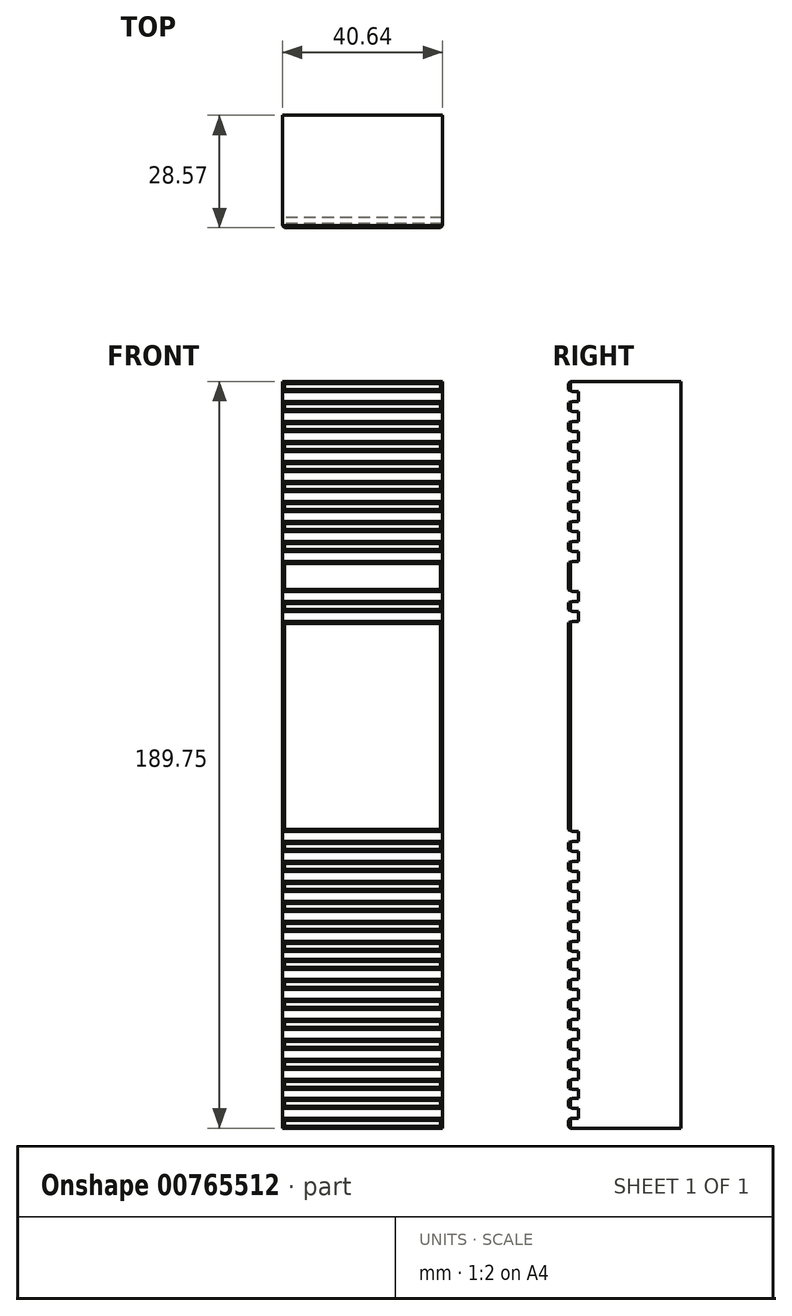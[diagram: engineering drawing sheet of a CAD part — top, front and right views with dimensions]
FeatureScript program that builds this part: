
annotation { "Feature Type Name" : "Feature", "Feature Type Description" : "" }
export const myFeature = defineFeature(function(context is Context, id is Id, definition is map)
    precondition{}
    {
        {
            var Q0;
            Q0=qCreatedBy(makeId("Top.planeOp"),FACE);
            var sketch = newSketch(context, id + "F0", { "sketchPlane" : qUnion([Q0])});
            skLineSegment(sketch, "E0.bottom", {"start": v(0, 0) * mm, "end": v(40.64, 0) * mm});
            skLineSegment(sketch, "E0.top", {"start": v(0, 35.56) * mm, "end": v(40.64, 35.56) * mm});
            skLineSegment(sketch, "E0.left", {"start": v(0, 0) * mm, "end": v(0, 35.56) * mm});
            skLineSegment(sketch, "E0.right", {"start": v(40.64, 0) * mm, "end": v(40.64, 35.56) * mm});
            skSolve(sketch);
        }
        {
            var Q0;
            Q0=makeQuery(id+"F0.imprint","IMPRINT",FACE,{"disambiguationData":[TD([[makeQuery(id+"F0.imprint","IMPRINT",EDGE,{"derivedFrom":sQuery(id+"F0.wireOp",EDGE,"E0.bottom")}),1.0]])]});
            extrude(context, id + "F1", {"entities" : qUnion([Q0]), "depth" : 190.5 * mm, "offsetDistance" : 25.4 * mm});
        }
        {
            var Q0;
            Q0=makeQuery(id+"F1.opExtrude","SWEPT_FACE",FACE,{"disambiguationData":[OSD([sQuery(id+"F0.wireOp",EDGE,"E0.left")])]});
            var sketch = newSketch(context, id + "F2", { "sketchPlane" : qUnion([Q0])});
            skLineSegment(sketch, "E1", {"start": v(0, 190.5) * mm, "end": v(-2.54, 190.5) * mm});
            skLineSegment(sketch, "E2", {"start": v(-2.54, 190.5) * mm, "end": v(-2.54, 0) * mm});
            skLineSegment(sketch, "E3", {"start": v(0, 190.5) * mm, "end": v(0, 185.42) * mm});
            skLineSegment(sketch, "E4", {"start": v(0, 185.42) * mm, "end": v(-2.54, 185.42) * mm});
            skLineSegment(sketch, "E5", {"start": v(0, 187.96) * mm, "end": v(-2.54, 187.96) * mm});
            skLineSegment(sketch, "E6", {"start": v(0, 185.42) * mm, "end": v(0, 175.26) * mm});
            skLineSegment(sketch, "E7", {"start": v(0, 175.26) * mm, "end": v(-2.54, 175.26) * mm});
            skLineSegment(sketch, "E8", {"start": v(0, 180.34) * mm, "end": v(-2.54, 180.34) * mm});
            skLineSegment(sketch, "E9", {"start": v(-2.54, 185.42) * mm, "end": v(-2.54, 182.88) * mm});
            skLineSegment(sketch, "E10", {"start": v(-2.54, 182.88) * mm, "end": v(0, 182.88) * mm});
            skLineSegment(sketch, "E11", {"start": v(0, 175.26) * mm, "end": v(0, 177.8) * mm});
            skLineSegment(sketch, "E12", {"start": v(0, 177.8) * mm, "end": v(-2.54, 177.8) * mm});
            skLineSegment(sketch, "E13", {"start": v(-2.54, 175.26) * mm, "end": v(-2.54, 170.18) * mm});
            skLineSegment(sketch, "E14", {"start": v(-2.54, 170.18) * mm, "end": v(0, 170.18) * mm});
            skLineSegment(sketch, "E15", {"start": v(0, 170.18) * mm, "end": v(0, 172.72) * mm});
            skPoint(sketch, "E15.endSnap0", {"position": v(-2.54, 172.72) * mm});
            skLineSegment(sketch, "E16", {"start": v(0, 172.72) * mm, "end": v(-2.54, 172.72) * mm});
            skLineSegment(sketch, "E17", {"start": v(-2.54, 170.18) * mm, "end": v(-2.54, 165.1) * mm});
            skLineSegment(sketch, "E18", {"start": v(-2.54, 165.1) * mm, "end": v(0, 165.1) * mm});
            skLineSegment(sketch, "E19", {"start": v(0, 165.1) * mm, "end": v(0, 167.64) * mm});
            skPoint(sketch, "E19.endSnap0", {"position": v(-2.54, 167.64) * mm});
            skLineSegment(sketch, "E20", {"start": v(0, 167.64) * mm, "end": v(-2.54, 167.64) * mm});
            skLineSegment(sketch, "E21", {"start": v(-2.54, 165.1) * mm, "end": v(-2.54, 160.02) * mm});
            skLineSegment(sketch, "E22", {"start": v(-2.54, 160.02) * mm, "end": v(0, 160.02) * mm});
            skLineSegment(sketch, "E23", {"start": v(0, 160.02) * mm, "end": v(0, 162.56) * mm});
            skPoint(sketch, "E23.endSnap0", {"position": v(-2.54, 162.56) * mm});
            skLineSegment(sketch, "E24", {"start": v(0, 162.56) * mm, "end": v(-2.54, 162.56) * mm});
            skLineSegment(sketch, "E25", {"start": v(-2.54, 160.02) * mm, "end": v(-2.54, 154.94) * mm});
            skLineSegment(sketch, "E26", {"start": v(-2.54, 154.94) * mm, "end": v(0, 154.94) * mm});
            skPoint(sketch, "E27.endSnap0", {"position": v(-2.54, 157.48) * mm});
            skLineSegment(sketch, "E28", {"start": v(0, 154.94) * mm, "end": v(0, 157.48) * mm});
            skLineSegment(sketch, "E29", {"start": v(0, 157.48) * mm, "end": v(-2.54, 157.48) * mm});
            skLineSegment(sketch, "E30", {"start": v(-2.54, 154.94) * mm, "end": v(-2.54, 149.86) * mm});
            skLineSegment(sketch, "E31", {"start": v(-2.54, 149.86) * mm, "end": v(0, 149.86) * mm});
            skLineSegment(sketch, "E32", {"start": v(0, 149.86) * mm, "end": v(0, 152.4) * mm});
            skPoint(sketch, "E32.endSnap0", {"position": v(-2.54, 152.4) * mm});
            skLineSegment(sketch, "E33", {"start": v(0, 152.4) * mm, "end": v(-2.54, 152.4) * mm});
            skLineSegment(sketch, "E34.MirrorCS", {"start": v(-2.54, 109.22) * mm, "end": v(-2.54, 299.72) * mm});
            skLineSegment(sketch, "E35.MirrorCS", {"start": v(0, 149.86) * mm, "end": v(0, 147.32) * mm});
            skLineSegment(sketch, "E36.MirrorCS", {"start": v(0, 142.24) * mm, "end": v(-2.54, 142.24) * mm});
            skLineSegment(sketch, "E37.MirrorCS", {"start": v(-2.54, 144.78) * mm, "end": v(0, 144.78) * mm});
            skLineSegment(sketch, "E38", {"start": v(0, 147.32) * mm, "end": v(-2.54, 147.32) * mm});
            skLineSegment(sketch, "E39.bottom", {"start": v(-2.54, 142.24) * mm, "end": v(0, 142.24) * mm});
            skLineSegment(sketch, "E39.top", {"start": v(-2.54, 139.7) * mm, "end": v(0, 139.7) * mm});
            skLineSegment(sketch, "E39.left", {"start": v(-2.54, 142.24) * mm, "end": v(-2.54, 139.7) * mm});
            skLineSegment(sketch, "E39.right", {"start": v(0, 142.24) * mm, "end": v(0, 139.7) * mm});
            skLineSegment(sketch, "E40.top", {"start": v(-2.54, 137.16) * mm, "end": v(0, 137.16) * mm});
            skLineSegment(sketch, "E40.left", {"start": v(-2.54, 139.7) * mm, "end": v(-2.54, 137.16) * mm});
            skLineSegment(sketch, "E40.right", {"start": v(0, 139.7) * mm, "end": v(0, 137.16) * mm});
            skLineSegment(sketch, "E41.top", {"start": v(-2.54, 134.62) * mm, "end": v(0, 134.62) * mm});
            skLineSegment(sketch, "E41.left", {"start": v(-2.54, 137.16) * mm, "end": v(-2.54, 134.62) * mm});
            skLineSegment(sketch, "E41.right", {"start": v(0, 137.16) * mm, "end": v(0, 134.62) * mm});
            skLineSegment(sketch, "E42.top", {"start": v(-2.54, 132.08) * mm, "end": v(0, 132.08) * mm});
            skLineSegment(sketch, "E42.left", {"start": v(-2.54, 134.62) * mm, "end": v(-2.54, 132.08) * mm});
            skLineSegment(sketch, "E42.right", {"start": v(0, 134.62) * mm, "end": v(0, 132.08) * mm});
            skLineSegment(sketch, "E43.top", {"start": v(-2.54, 129.54) * mm, "end": v(0, 129.54) * mm});
            skLineSegment(sketch, "E43.left", {"start": v(-2.54, 132.08) * mm, "end": v(-2.54, 129.54) * mm});
            skLineSegment(sketch, "E43.right", {"start": v(0, 132.08) * mm, "end": v(0, 129.54) * mm});
            skLineSegment(sketch, "E44", {"start": v(-2.54, 129.54) * mm, "end": v(-2.54, 127) * mm});
            skLineSegment(sketch, "E45", {"start": v(-2.54, 127) * mm, "end": v(-2.54, 124.46) * mm});
            skLineSegment(sketch, "E46", {"start": v(-2.54, 124.46) * mm, "end": v(-2.54, 121.92) * mm});
            skLineSegment(sketch, "E47", {"start": v(-2.54, 121.92) * mm, "end": v(-2.54, 119.38) * mm});
            skLineSegment(sketch, "E48", {"start": v(-2.54, 119.38) * mm, "end": v(-2.54, 116.84) * mm});
            skLineSegment(sketch, "E49", {"start": v(-2.54, 116.84) * mm, "end": v(-2.54, 114.3) * mm});
            skLineSegment(sketch, "E50", {"start": v(-2.54, 114.3) * mm, "end": v(-2.54, 111.76) * mm});
            skLineSegment(sketch, "E51", {"start": v(-2.54, 111.76) * mm, "end": v(-2.54, 109.22) * mm});
            skLineSegment(sketch, "E52", {"start": v(-2.54, 127) * mm, "end": v(0, 127) * mm});
            skLineSegment(sketch, "E53", {"start": v(0, 127) * mm, "end": v(0, 124.46) * mm});
            skLineSegment(sketch, "E54", {"start": v(0, 124.46) * mm, "end": v(-2.54, 124.46) * mm});
            skLineSegment(sketch, "E55", {"start": v(-2.54, 121.92) * mm, "end": v(0, 121.92) * mm});
            skLineSegment(sketch, "E56", {"start": v(0, 121.92) * mm, "end": v(0, 119.38) * mm});
            skLineSegment(sketch, "E57", {"start": v(0, 119.38) * mm, "end": v(-2.54, 119.38) * mm});
            skLineSegment(sketch, "E58", {"start": v(-2.54, 116.84) * mm, "end": v(0, 116.84) * mm});
            skLineSegment(sketch, "E59", {"start": v(0, 116.84) * mm, "end": v(0, 114.3) * mm});
            skLineSegment(sketch, "E60", {"start": v(0, 114.3) * mm, "end": v(-2.54, 114.3) * mm});
            skLineSegment(sketch, "E61", {"start": v(-2.54, 111.76) * mm, "end": v(0, 111.76) * mm});
            skLineSegment(sketch, "E62", {"start": v(0, 111.76) * mm, "end": v(0, 109.22) * mm});
            skLineSegment(sketch, "E63", {"start": v(0, 109.22) * mm, "end": v(-2.54, 109.22) * mm});
            skLineSegment(sketch, "E64.MirrorCS", {"start": v(-2.54, 58.42) * mm, "end": v(0, 58.42) * mm});
            skLineSegment(sketch, "E65", {"start": v(-2.54, 109.22) * mm, "end": v(-2.54, 106.68) * mm});
            skLineSegment(sketch, "E66", {"start": v(-2.54, 106.68) * mm, "end": v(-2.54, 104.14) * mm});
            skLineSegment(sketch, "E67", {"start": v(-2.54, 104.14) * mm, "end": v(-2.54, 101.6) * mm});
            skLineSegment(sketch, "E68", {"start": v(-2.54, 101.6) * mm, "end": v(-2.54, 99.06) * mm});
            skLineSegment(sketch, "E69", {"start": v(-2.54, 99.06) * mm, "end": v(-2.54, 96.52) * mm});
            skLineSegment(sketch, "E70", {"start": v(-2.54, 96.52) * mm, "end": v(-2.54, 93.98) * mm});
            skLineSegment(sketch, "E71", {"start": v(-2.54, 93.98) * mm, "end": v(-2.54, 91.44) * mm});
            skLineSegment(sketch, "E72", {"start": v(-2.54, 91.44) * mm, "end": v(-2.54, 88.9) * mm});
            skLineSegment(sketch, "E73", {"start": v(-2.54, 88.9) * mm, "end": v(-2.54, 86.36) * mm});
            skLineSegment(sketch, "E74", {"start": v(-2.54, 86.36) * mm, "end": v(-2.54, 83.82) * mm});
            skLineSegment(sketch, "E75", {"start": v(-2.54, 83.82) * mm, "end": v(-2.54, 81.28) * mm});
            skLineSegment(sketch, "E76", {"start": v(-2.54, 81.28) * mm, "end": v(-2.54, 78.74) * mm});
            skLineSegment(sketch, "E77", {"start": v(-2.54, 78.74) * mm, "end": v(-2.54, 76.2) * mm});
            skLineSegment(sketch, "E78", {"start": v(0, 109.22) * mm, "end": v(0, 76.2) * mm});
            skLineSegment(sketch, "E79", {"start": v(-2.54, 76.2) * mm, "end": v(0, 76.2) * mm});
            skLineSegment(sketch, "E80", {"start": v(-2.54, 78.74) * mm, "end": v(0, 78.74) * mm});
            skLineSegment(sketch, "E81", {"start": v(-2.54, 81.28) * mm, "end": v(0, 81.28) * mm});
            skLineSegment(sketch, "E82", {"start": v(-2.54, 83.82) * mm, "end": v(0, 83.82) * mm});
            skLineSegment(sketch, "E83", {"start": v(-2.54, 86.36) * mm, "end": v(0, 86.36) * mm});
            skLineSegment(sketch, "E84", {"start": v(0, 86.36) * mm, "end": v(0, 88.9) * mm});
            skLineSegment(sketch, "E85", {"start": v(0, 88.9) * mm, "end": v(-2.54, 88.9) * mm});
            skLineSegment(sketch, "E86", {"start": v(-2.54, 91.44) * mm, "end": v(0, 91.44) * mm});
            skLineSegment(sketch, "E87", {"start": v(0, 91.44) * mm, "end": v(0, 93.98) * mm});
            skLineSegment(sketch, "E88", {"start": v(0, 93.98) * mm, "end": v(-2.54, 93.98) * mm});
            skLineSegment(sketch, "E89", {"start": v(-2.54, 96.52) * mm, "end": v(0, 96.52) * mm});
            skLineSegment(sketch, "E90", {"start": v(0, 96.52) * mm, "end": v(0, 99.06) * mm});
            skLineSegment(sketch, "E91", {"start": v(0, 99.06) * mm, "end": v(-2.54, 99.06) * mm});
            skLineSegment(sketch, "E92", {"start": v(-2.54, 101.6) * mm, "end": v(0, 101.6) * mm});
            skLineSegment(sketch, "E93", {"start": v(0, 101.6) * mm, "end": v(0, 104.14) * mm});
            skLineSegment(sketch, "E94", {"start": v(0, 104.14) * mm, "end": v(-2.54, 104.14) * mm});
            skLineSegment(sketch, "E95", {"start": v(-2.54, 106.68) * mm, "end": v(0, 106.68) * mm});
            skLineSegment(sketch, "E96", {"start": v(-2.54, 76.2) * mm, "end": v(-2.54, 73.66) * mm});
            skLineSegment(sketch, "E97", {"start": v(-2.54, 73.66) * mm, "end": v(0, 73.66) * mm});
            skLineSegment(sketch, "E98", {"start": v(0, 73.66) * mm, "end": v(0, 71.12) * mm});
            skLineSegment(sketch, "E99", {"start": v(0, 71.12) * mm, "end": v(-2.54, 71.12) * mm});
            skLineSegment(sketch, "E100", {"start": v(-2.54, 71.12) * mm, "end": v(-2.54, 68.58) * mm});
            skLineSegment(sketch, "E101", {"start": v(-2.54, 68.58) * mm, "end": v(0, 68.58) * mm});
            skLineSegment(sketch, "E102", {"start": v(0, 68.58) * mm, "end": v(0, 66.04) * mm});
            skLineSegment(sketch, "E103", {"start": v(0, 66.04) * mm, "end": v(-2.54, 66.04) * mm});
            skLineSegment(sketch, "E104", {"start": v(-2.54, 66.04) * mm, "end": v(-2.54, 63.5) * mm});
            skLineSegment(sketch, "E105", {"start": v(-2.54, 63.5) * mm, "end": v(0, 63.5) * mm});
            skLineSegment(sketch, "E106", {"start": v(0, 63.5) * mm, "end": v(0, 60.96) * mm});
            skLineSegment(sketch, "E107", {"start": v(0, 60.96) * mm, "end": v(-2.54, 60.96) * mm});
            skLineSegment(sketch, "E108", {"start": v(-2.54, 58.42) * mm, "end": v(-2.54, 55.88) * mm});
            skLineSegment(sketch, "E109", {"start": v(-2.54, 55.88) * mm, "end": v(0, 55.88) * mm});
            skLineSegment(sketch, "E110", {"start": v(0, 55.88) * mm, "end": v(0, 53.34) * mm});
            skLineSegment(sketch, "E111", {"start": v(0, 53.34) * mm, "end": v(-2.54, 53.34) * mm});
            skLineSegment(sketch, "E112", {"start": v(-2.54, 53.34) * mm, "end": v(-2.54, 50.8) * mm});
            skLineSegment(sketch, "E113", {"start": v(-2.54, 50.8) * mm, "end": v(0, 50.8) * mm});
            skLineSegment(sketch, "E114", {"start": v(0, 50.8) * mm, "end": v(0, 48.26) * mm});
            skLineSegment(sketch, "E115", {"start": v(0, 48.26) * mm, "end": v(-2.54, 48.26) * mm});
            skLineSegment(sketch, "E116", {"start": v(-2.54, 48.26) * mm, "end": v(-2.54, 45.72) * mm});
            skLineSegment(sketch, "E117", {"start": v(-2.54, 45.72) * mm, "end": v(0, 45.72) * mm});
            skLineSegment(sketch, "E118", {"start": v(0, 45.72) * mm, "end": v(0, 43.57) * mm});
            skLineSegment(sketch, "E119", {"start": v(0, 43.57) * mm, "end": v(-2.54, 43.57) * mm});
            skLineSegment(sketch, "E120", {"start": v(-2.54, 43.57) * mm, "end": v(-2.54, 41.03) * mm});
            skLineSegment(sketch, "E121", {"start": v(-2.54, 41.03) * mm, "end": v(0, 41.03) * mm});
            skLineSegment(sketch, "E122", {"start": v(0, 41.03) * mm, "end": v(0, 38.49) * mm});
            skLineSegment(sketch, "E123", {"start": v(0, 38.49) * mm, "end": v(-2.54, 38.49) * mm});
            skLineSegment(sketch, "E124", {"start": v(-2.54, 38.49) * mm, "end": v(-2.54, 35.95) * mm});
            skLineSegment(sketch, "E125", {"start": v(-2.54, 35.95) * mm, "end": v(0, 35.95) * mm});
            skLineSegment(sketch, "E126", {"start": v(0, 35.95) * mm, "end": v(0, 33.4) * mm});
            skLineSegment(sketch, "E127", {"start": v(0, 33.4) * mm, "end": v(-2.54, 33.4) * mm});
            skLineSegment(sketch, "E128", {"start": v(-2.54, 33.4) * mm, "end": v(-2.54, 30.87) * mm});
            skLineSegment(sketch, "E129", {"start": v(-2.54, 30.87) * mm, "end": v(0, 30.87) * mm});
            skLineSegment(sketch, "E130", {"start": v(0, 30.87) * mm, "end": v(0, 28.33) * mm});
            skLineSegment(sketch, "E131", {"start": v(0, 28.33) * mm, "end": v(-2.54, 28.33) * mm});
            skLineSegment(sketch, "E132", {"start": v(-2.54, 28.33) * mm, "end": v(-2.54, 25.79) * mm});
            skLineSegment(sketch, "E133", {"start": v(-2.54, 25.79) * mm, "end": v(0, 25.79) * mm});
            skLineSegment(sketch, "E134", {"start": v(0, 25.79) * mm, "end": v(0, 23.25) * mm});
            skLineSegment(sketch, "E135", {"start": v(0, 23.25) * mm, "end": v(-2.54, 23.25) * mm});
            skLineSegment(sketch, "E136", {"start": v(-2.54, 23.25) * mm, "end": v(-2.54, 20.7) * mm});
            skLineSegment(sketch, "E137", {"start": v(-2.54, 20.7) * mm, "end": v(0, 20.7) * mm});
            skLineSegment(sketch, "E138", {"start": v(0, 20.7) * mm, "end": v(0, 18.17) * mm});
            skLineSegment(sketch, "E139", {"start": v(0, 18.17) * mm, "end": v(-2.54, 18.17) * mm});
            skLineSegment(sketch, "E140", {"start": v(-2.54, 18.17) * mm, "end": v(-2.54, 15.63) * mm});
            skLineSegment(sketch, "E141", {"start": v(-2.54, 15.63) * mm, "end": v(0, 15.63) * mm});
            skLineSegment(sketch, "E142", {"start": v(0, 15.63) * mm, "end": v(0, 13.09) * mm});
            skLineSegment(sketch, "E143", {"start": v(0, 13.09) * mm, "end": v(-2.54, 13.09) * mm});
            skLineSegment(sketch, "E144", {"start": v(-2.54, 13.09) * mm, "end": v(-2.54, 10.55) * mm});
            skLineSegment(sketch, "E145", {"start": v(-2.54, 10.55) * mm, "end": v(0, 10.55) * mm});
            skLineSegment(sketch, "E146", {"start": v(0, 10.55) * mm, "end": v(0, 8.37) * mm});
            skLineSegment(sketch, "E147", {"start": v(0, 8.37) * mm, "end": v(-2.54, 8.37) * mm});
            skLineSegment(sketch, "E148", {"start": v(-2.54, 8.37) * mm, "end": v(-2.54, 5.83) * mm});
            skLineSegment(sketch, "E149", {"start": v(-2.54, 5.83) * mm, "end": v(0, 5.83) * mm});
            skLineSegment(sketch, "E150", {"start": v(0, 5.83) * mm, "end": v(0, 3.3) * mm});
            skLineSegment(sketch, "E151", {"start": v(0, 3.3) * mm, "end": v(-2.54, 3.3) * mm});
            skSolve(sketch);
        }
        {
            var Q0;
            {var subQ0=sQuery(id+"F2.wireOp",EDGE,"E4");Q0=makeQuery(id+"F2.imprint","IMPRINT",FACE,{"disambiguationData":[TD([[makeQuery(id+"F2.imprint","IMPRINT",EDGE,{"derivedFrom":subQ0}),-1.0]])]});}
            var Q1;
            {var subQ0=sQuery(id+"F2.wireOp",EDGE,"E8");Q1=makeQuery(id+"F2.imprint","IMPRINT",FACE,{"disambiguationData":[TD([[makeQuery(id+"F2.imprint","IMPRINT",EDGE,{"derivedFrom":subQ0}),-1.0]])]});}
            var Q2;
            {var subQ0=sQuery(id+"F2.wireOp",EDGE,"E7");Q2=makeQuery(id+"F2.imprint","IMPRINT",FACE,{"disambiguationData":[TD([[makeQuery(id+"F2.imprint","IMPRINT",EDGE,{"derivedFrom":subQ0}),-1.0]])]});}
            var Q3;
            {var subQ0=sQuery(id+"F2.wireOp",EDGE,"E14");Q3=makeQuery(id+"F2.imprint","IMPRINT",FACE,{"disambiguationData":[TD([[makeQuery(id+"F2.imprint","IMPRINT",EDGE,{"derivedFrom":subQ0}),1.0]])]});}
            var Q4;
            {var subQ0=sQuery(id+"F2.wireOp",EDGE,"E18");Q4=makeQuery(id+"F2.imprint","IMPRINT",FACE,{"disambiguationData":[TD([[makeQuery(id+"F2.imprint","IMPRINT",EDGE,{"derivedFrom":subQ0}),1.0]])]});}
            var Q5;
            {var subQ0=sQuery(id+"F2.wireOp",EDGE,"E22");Q5=makeQuery(id+"F2.imprint","IMPRINT",FACE,{"disambiguationData":[TD([[makeQuery(id+"F2.imprint","IMPRINT",EDGE,{"derivedFrom":subQ0}),1.0]])]});}
            var Q6;
            {var subQ0=sQuery(id+"F2.wireOp",EDGE,"E26");Q6=makeQuery(id+"F2.imprint","IMPRINT",FACE,{"disambiguationData":[TD([[makeQuery(id+"F2.imprint","IMPRINT",EDGE,{"derivedFrom":subQ0}),1.0]])]});}
            var Q7;
            {var subQ0=sQuery(id+"F2.wireOp",EDGE,"E31");Q7=makeQuery(id+"F2.imprint","IMPRINT",FACE,{"disambiguationData":[TD([[makeQuery(id+"F2.imprint","IMPRINT",EDGE,{"derivedFrom":subQ0}),1.0]])]});}
            var Q8;
            {var subQ0=sQuery(id+"F2.wireOp",EDGE,"E37.MirrorCS");Q8=makeQuery(id+"F2.imprint","IMPRINT",FACE,{"disambiguationData":[TD([[makeQuery(id+"F2.imprint","IMPRINT",EDGE,{"derivedFrom":subQ0}),1.0]])]});}
            var Q9;
            Q9=makeQuery(id+"F2.imprint","IMPRINT",FACE,{"disambiguationData":[TD([[makeQuery(id+"F2.imprint","IMPRINT",EDGE,{"derivedFrom":sQuery(id+"F2.wireOp",EDGE,"E39.bottom")}),-1.0]])]});
            var Q10;
            Q10=makeQuery(id+"F2.imprint","IMPRINT",FACE,{"disambiguationData":[TD([[makeQuery(id+"F2.imprint","IMPRINT",EDGE,{"derivedFrom":sQuery(id+"F2.wireOp",EDGE,"E40.top")}),-1.0]])]});
            var Q11;
            Q11=makeQuery(id+"F2.imprint","IMPRINT",FACE,{"disambiguationData":[TD([[makeQuery(id+"F2.imprint","IMPRINT",EDGE,{"derivedFrom":sQuery(id+"F2.wireOp",EDGE,"E42.top")}),-1.0]])]});
            var Q12;
            Q12=makeQuery(id+"F2.imprint","IMPRINT",FACE,{"disambiguationData":[TD([[makeQuery(id+"F2.imprint","IMPRINT",EDGE,{"derivedFrom":sQuery(id+"F2.wireOp",EDGE,"E45")}),1.0]])]});
            var Q13;
            Q13=makeQuery(id+"F2.imprint","IMPRINT",FACE,{"disambiguationData":[TD([[makeQuery(id+"F2.imprint","IMPRINT",EDGE,{"derivedFrom":sQuery(id+"F2.wireOp",EDGE,"E47")}),1.0]])]});
            var Q14;
            Q14=makeQuery(id+"F2.imprint","IMPRINT",FACE,{"disambiguationData":[TD([[makeQuery(id+"F2.imprint","IMPRINT",EDGE,{"derivedFrom":sQuery(id+"F2.wireOp",EDGE,"E49")}),1.0]])]});
            var Q15;
            Q15=makeQuery(id+"F2.imprint","IMPRINT",FACE,{"disambiguationData":[TD([[makeQuery(id+"F2.imprint","IMPRINT",EDGE,{"derivedFrom":sQuery(id+"F2.wireOp",EDGE,"E51")}),1.0]])]});
            var Q16;
            Q16=makeQuery(id+"F2.imprint","IMPRINT",FACE,{"disambiguationData":[TD([[makeQuery(id+"F2.imprint","IMPRINT",EDGE,{"derivedFrom":sQuery(id+"F2.wireOp",EDGE,"E66")}),1.0]])]});
            var Q17;
            Q17=makeQuery(id+"F2.imprint","IMPRINT",FACE,{"disambiguationData":[TD([[makeQuery(id+"F2.imprint","IMPRINT",EDGE,{"derivedFrom":sQuery(id+"F2.wireOp",EDGE,"E68")}),1.0]])]});
            var Q18;
            Q18=makeQuery(id+"F2.imprint","IMPRINT",FACE,{"disambiguationData":[TD([[makeQuery(id+"F2.imprint","IMPRINT",EDGE,{"derivedFrom":sQuery(id+"F2.wireOp",EDGE,"E70")}),1.0]])]});
            var Q19;
            Q19=makeQuery(id+"F2.imprint","IMPRINT",FACE,{"disambiguationData":[TD([[makeQuery(id+"F2.imprint","IMPRINT",EDGE,{"derivedFrom":sQuery(id+"F2.wireOp",EDGE,"E72")}),1.0]])]});
            var Q20;
            Q20=makeQuery(id+"F2.imprint","IMPRINT",FACE,{"disambiguationData":[TD([[makeQuery(id+"F2.imprint","IMPRINT",EDGE,{"derivedFrom":sQuery(id+"F2.wireOp",EDGE,"E74")}),1.0]])]});
            var Q21;
            Q21=makeQuery(id+"F2.imprint","IMPRINT",FACE,{"disambiguationData":[TD([[makeQuery(id+"F2.imprint","IMPRINT",EDGE,{"derivedFrom":sQuery(id+"F2.wireOp",EDGE,"E76")}),1.0]])]});
            var Q22;
            {var subQ0=sQuery(id+"F2.wireOp",EDGE,"E79");Q22=makeQuery(id+"F2.imprint","IMPRINT",FACE,{"disambiguationData":[TD([[makeQuery(id+"F2.imprint","IMPRINT",EDGE,{"derivedFrom":subQ0}),-1.0]])]});}
            var Q23;
            {var subQ0=sQuery(id+"F2.wireOp",EDGE,"E99");Q23=makeQuery(id+"F2.imprint","IMPRINT",FACE,{"disambiguationData":[TD([[makeQuery(id+"F2.imprint","IMPRINT",EDGE,{"derivedFrom":subQ0}),1.0]])]});}
            var Q24;
            {var subQ0=sQuery(id+"F2.wireOp",EDGE,"E103");Q24=makeQuery(id+"F2.imprint","IMPRINT",FACE,{"disambiguationData":[TD([[makeQuery(id+"F2.imprint","IMPRINT",EDGE,{"derivedFrom":subQ0}),1.0]])]});}
            var Q25;
            {var subQ0=sQuery(id+"F2.wireOp",EDGE,"E64.MirrorCS");Q25=makeQuery(id+"F2.imprint","IMPRINT",FACE,{"disambiguationData":[TD([[makeQuery(id+"F2.imprint","IMPRINT",EDGE,{"derivedFrom":subQ0}),1.0]])]});}
            var Q26;
            {var subQ0=sQuery(id+"F2.wireOp",EDGE,"E109");Q26=makeQuery(id+"F2.imprint","IMPRINT",FACE,{"disambiguationData":[TD([[makeQuery(id+"F2.imprint","IMPRINT",EDGE,{"derivedFrom":subQ0}),-1.0]])]});}
            var Q27;
            {var subQ0=sQuery(id+"F2.wireOp",EDGE,"E113");Q27=makeQuery(id+"F2.imprint","IMPRINT",FACE,{"disambiguationData":[TD([[makeQuery(id+"F2.imprint","IMPRINT",EDGE,{"derivedFrom":subQ0}),-1.0]])]});}
            var Q28;
            {var subQ0=sQuery(id+"F2.wireOp",EDGE,"E117");Q28=makeQuery(id+"F2.imprint","IMPRINT",FACE,{"disambiguationData":[TD([[makeQuery(id+"F2.imprint","IMPRINT",EDGE,{"derivedFrom":subQ0}),-1.0]])]});}
            var Q29;
            {var subQ0=sQuery(id+"F2.wireOp",EDGE,"E121");Q29=makeQuery(id+"F2.imprint","IMPRINT",FACE,{"disambiguationData":[TD([[makeQuery(id+"F2.imprint","IMPRINT",EDGE,{"derivedFrom":subQ0}),-1.0]])]});}
            var Q30;
            {var subQ0=sQuery(id+"F2.wireOp",EDGE,"E125");Q30=makeQuery(id+"F2.imprint","IMPRINT",FACE,{"disambiguationData":[TD([[makeQuery(id+"F2.imprint","IMPRINT",EDGE,{"derivedFrom":subQ0}),-1.0]])]});}
            var Q31;
            {var subQ0=sQuery(id+"F2.wireOp",EDGE,"E129");Q31=makeQuery(id+"F2.imprint","IMPRINT",FACE,{"disambiguationData":[TD([[makeQuery(id+"F2.imprint","IMPRINT",EDGE,{"derivedFrom":subQ0}),-1.0]])]});}
            var Q32;
            {var subQ0=sQuery(id+"F2.wireOp",EDGE,"E133");Q32=makeQuery(id+"F2.imprint","IMPRINT",FACE,{"disambiguationData":[TD([[makeQuery(id+"F2.imprint","IMPRINT",EDGE,{"derivedFrom":subQ0}),-1.0]])]});}
            var Q33;
            {var subQ0=sQuery(id+"F2.wireOp",EDGE,"E137");Q33=makeQuery(id+"F2.imprint","IMPRINT",FACE,{"disambiguationData":[TD([[makeQuery(id+"F2.imprint","IMPRINT",EDGE,{"derivedFrom":subQ0}),-1.0]])]});}
            var Q34;
            {var subQ0=sQuery(id+"F2.wireOp",EDGE,"E141");Q34=makeQuery(id+"F2.imprint","IMPRINT",FACE,{"disambiguationData":[TD([[makeQuery(id+"F2.imprint","IMPRINT",EDGE,{"derivedFrom":subQ0}),-1.0]])]});}
            var Q35;
            {var subQ0=sQuery(id+"F2.wireOp",EDGE,"E145");Q35=makeQuery(id+"F2.imprint","IMPRINT",FACE,{"disambiguationData":[TD([[makeQuery(id+"F2.imprint","IMPRINT",EDGE,{"derivedFrom":subQ0}),-1.0]])]});}
            var Q36;
            {var subQ0=sQuery(id+"F2.wireOp",EDGE,"E149");Q36=makeQuery(id+"F2.imprint","IMPRINT",FACE,{"disambiguationData":[TD([[makeQuery(id+"F2.imprint","IMPRINT",EDGE,{"derivedFrom":subQ0}),-1.0]])]});}
            extrude(context, id + "F3", {"entities" : qUnion([Q0, Q1, Q2, Q3, Q4, Q5, Q6, Q7, Q8, Q9, Q10, Q11, Q12, Q13, Q14, Q15, Q16, Q17, Q18, Q19, Q20, Q21, Q22, Q23, Q24, Q25, Q26, Q27, Q28, Q29, Q30, Q31, Q32, Q33, Q34, Q35, Q36]), "operationType" : NewBodyOperationType.REMOVE, "endBound" : BoundingType.THROUGH_ALL, "oppositeDirection" : true, "depth" : 25.4 * mm, "offsetDistance" : 25.4 * mm});
        }
        {
            var Q0;
            Q0=makeQuery(id+"F1.opExtrude","SWEPT_FACE",FACE,{"disambiguationData":[OSD([sQuery(id+"F0.wireOp",EDGE,"E0.top")])]});
            extrude(context, id + "F4", {"entities" : qUnion([Q0]), "operationType" : NewBodyOperationType.REMOVE, "oppositeDirection" : true, "depth" : 5.08 * mm, "offsetDistance" : 25.4 * mm});
        }
        {
            var Q0;
            Q0=makeQuery(id+"F4.boolean.opBoolean","COPY",FACE,{"derivedFrom":makeQuery(id+"F4.opExtrude","CAP_FACE",FACE,{"disambiguationData":[OSD([sQuery(id+"F0.wireOp",EDGE,"E0.top")])],"isStart":false})});
            extrude(context, id + "F5", {"entities" : qUnion([Q0]), "operationType" : NewBodyOperationType.REMOVE, "oppositeDirection" : true, "depth" : 1.9 * mm, "offsetDistance" : 25.4 * mm});
        }
        {
            var Q0;
            Q0=makeQuery(id+"F1.opExtrude","CAP_EDGE",EDGE,{"disambiguationData":[OSD([sQuery(id+"F0.wireOp",EDGE,"E0.bottom")])],"isStart":false});
            var Q1;
            Q1=makeQuery(id+"F3.boolean.opBoolean","COPY",EDGE,{"derivedFrom":makeQuery(id+"F3.opExtrude","SWEPT_EDGE",EDGE,{"disambiguationData":[OSD([sQuery(id+"F2.wireOp",EDGE,"E3"),sQuery(id+"F2.wireOp",EDGE,"E5")])]})});
            var Q2;
            Q2=makeQuery(id+"F3.boolean.opBoolean","COPY",EDGE,{"derivedFrom":makeQuery(id+"F3.opExtrude","SWEPT_EDGE",EDGE,{"disambiguationData":[OSD([sQuery(id+"F2.wireOp",EDGE,"E3"),sQuery(id+"F2.wireOp",EDGE,"E4"),sQuery(id+"F2.wireOp",EDGE,"E6")])]})});
            var Q3;
            Q3=makeQuery(id+"F3.boolean.opBoolean","COPY",EDGE,{"derivedFrom":makeQuery(id+"F3.opExtrude","SWEPT_EDGE",EDGE,{"disambiguationData":[OSD([sQuery(id+"F2.wireOp",EDGE,"E6"),sQuery(id+"F2.wireOp",EDGE,"E10")])]})});
            var Q4;
            Q4=makeQuery(id+"F3.boolean.opBoolean","COPY",EDGE,{"derivedFrom":makeQuery(id+"F3.opExtrude","SWEPT_EDGE",EDGE,{"disambiguationData":[OSD([sQuery(id+"F2.wireOp",EDGE,"E6"),sQuery(id+"F2.wireOp",EDGE,"E8")])]})});
            var Q5;
            Q5=makeQuery(id+"F3.boolean.opBoolean","COPY",EDGE,{"derivedFrom":makeQuery(id+"F3.opExtrude","SWEPT_EDGE",EDGE,{"disambiguationData":[OSD([sQuery(id+"F2.wireOp",EDGE,"E6"),sQuery(id+"F2.wireOp",EDGE,"E11"),sQuery(id+"F2.wireOp",EDGE,"E12")])]})});
            var Q6;
            {var subQ2=sQuery(id+"F0.wireOp",EDGE,"E0.bottom");Q6=makeQuery(id+"F3.boolean.opBoolean","SPLIT",FACE,{"disambiguationData":[TD([makeQuery(id+"F3.opExtrude","SWEPT_FACE",FACE,{"disambiguationData":[OSD([sQuery(id+"F2.wireOp",EDGE,"E5")])]})])],"derivedFrom":makeQuery(id+"F1.opExtrude","SWEPT_FACE",FACE,{"disambiguationData":[OSD([subQ2])]})});}
            var Q7;
            Q7=makeQuery(id+"F3.boolean.opBoolean","SPLIT",FACE,{"disambiguationData":[TD([makeQuery(id+"F3.opExtrude","SWEPT_FACE",FACE,{"disambiguationData":[OSD([sQuery(id+"F2.wireOp",EDGE,"E4")])]})])],"derivedFrom":makeQuery(id+"F1.opExtrude","SWEPT_FACE",FACE,{"disambiguationData":[OSD([sQuery(id+"F0.wireOp",EDGE,"E0.bottom")])]})});
            var Q8;
            Q8=makeQuery(id+"F3.boolean.opBoolean","SPLIT",FACE,{"disambiguationData":[TD([makeQuery(id+"F3.opExtrude","SWEPT_FACE",FACE,{"disambiguationData":[OSD([sQuery(id+"F2.wireOp",EDGE,"E8")])]})])],"derivedFrom":makeQuery(id+"F1.opExtrude","SWEPT_FACE",FACE,{"disambiguationData":[OSD([sQuery(id+"F0.wireOp",EDGE,"E0.bottom")])]})});
            var Q9;
            Q9=makeQuery(id+"F3.boolean.opBoolean","SPLIT",FACE,{"disambiguationData":[TD([makeQuery(id+"F3.opExtrude","SWEPT_FACE",FACE,{"disambiguationData":[OSD([sQuery(id+"F2.wireOp",EDGE,"E7")])]})])],"derivedFrom":makeQuery(id+"F1.opExtrude","SWEPT_FACE",FACE,{"disambiguationData":[OSD([sQuery(id+"F0.wireOp",EDGE,"E0.bottom")])]})});
            var Q10;
            Q10=makeQuery(id+"F3.boolean.opBoolean","SPLIT",FACE,{"disambiguationData":[TD([makeQuery(id+"F3.opExtrude","SWEPT_FACE",FACE,{"disambiguationData":[OSD([sQuery(id+"F2.wireOp",EDGE,"E14")])]})])],"derivedFrom":makeQuery(id+"F1.opExtrude","SWEPT_FACE",FACE,{"disambiguationData":[OSD([sQuery(id+"F0.wireOp",EDGE,"E0.bottom")])]})});
            var Q11;
            Q11=makeQuery(id+"F3.boolean.opBoolean","SPLIT",FACE,{"disambiguationData":[TD([makeQuery(id+"F3.opExtrude","SWEPT_FACE",FACE,{"disambiguationData":[OSD([sQuery(id+"F2.wireOp",EDGE,"E18")])]})])],"derivedFrom":makeQuery(id+"F1.opExtrude","SWEPT_FACE",FACE,{"disambiguationData":[OSD([sQuery(id+"F0.wireOp",EDGE,"E0.bottom")])]})});
            var Q12;
            Q12=makeQuery(id+"F3.boolean.opBoolean","SPLIT",FACE,{"disambiguationData":[TD([makeQuery(id+"F3.opExtrude","SWEPT_FACE",FACE,{"disambiguationData":[OSD([sQuery(id+"F2.wireOp",EDGE,"E22")])]})])],"derivedFrom":makeQuery(id+"F1.opExtrude","SWEPT_FACE",FACE,{"disambiguationData":[OSD([sQuery(id+"F0.wireOp",EDGE,"E0.bottom")])]})});
            var Q13;
            Q13=makeQuery(id+"F3.boolean.opBoolean","SPLIT",FACE,{"disambiguationData":[TD([makeQuery(id+"F3.opExtrude","SWEPT_FACE",FACE,{"disambiguationData":[OSD([sQuery(id+"F2.wireOp",EDGE,"E26")])]})])],"derivedFrom":makeQuery(id+"F1.opExtrude","SWEPT_FACE",FACE,{"disambiguationData":[OSD([sQuery(id+"F0.wireOp",EDGE,"E0.bottom")])]})});
            var Q14;
            Q14=makeQuery(id+"F3.boolean.opBoolean","SPLIT",FACE,{"disambiguationData":[TD([makeQuery(id+"F3.opExtrude","SWEPT_FACE",FACE,{"disambiguationData":[OSD([sQuery(id+"F2.wireOp",EDGE,"E31")])]})])],"derivedFrom":makeQuery(id+"F1.opExtrude","SWEPT_FACE",FACE,{"disambiguationData":[OSD([sQuery(id+"F0.wireOp",EDGE,"E0.bottom")])]})});
            var Q15;
            Q15=makeQuery(id+"F3.boolean.opBoolean","SPLIT",FACE,{"disambiguationData":[TD([makeQuery(id+"F3.opExtrude","SWEPT_FACE",FACE,{"disambiguationData":[OSD([sQuery(id+"F2.wireOp",EDGE,"E37.MirrorCS")])]})])],"derivedFrom":makeQuery(id+"F1.opExtrude","SWEPT_FACE",FACE,{"disambiguationData":[OSD([sQuery(id+"F0.wireOp",EDGE,"E0.bottom")])]})});
            var Q16;
            Q16=makeQuery(id+"F3.boolean.opBoolean","SPLIT",FACE,{"disambiguationData":[TD([makeQuery(id+"F3.opExtrude","SWEPT_FACE",FACE,{"disambiguationData":[OSD([sQuery(id+"F2.wireOp",EDGE,"E39.top")])]})])],"derivedFrom":makeQuery(id+"F1.opExtrude","SWEPT_FACE",FACE,{"disambiguationData":[OSD([sQuery(id+"F0.wireOp",EDGE,"E0.bottom")])]})});
            var Q17;
            Q17=makeQuery(id+"F3.boolean.opBoolean","SPLIT",FACE,{"disambiguationData":[TD([makeQuery(id+"F3.opExtrude","SWEPT_FACE",FACE,{"disambiguationData":[OSD([sQuery(id+"F2.wireOp",EDGE,"E41.top")])]})])],"derivedFrom":makeQuery(id+"F1.opExtrude","SWEPT_FACE",FACE,{"disambiguationData":[OSD([sQuery(id+"F0.wireOp",EDGE,"E0.bottom")])]})});
            var Q18;
            Q18=makeQuery(id+"F3.boolean.opBoolean","SPLIT",FACE,{"disambiguationData":[TD([makeQuery(id+"F3.opExtrude","SWEPT_FACE",FACE,{"disambiguationData":[OSD([sQuery(id+"F2.wireOp",EDGE,"E43.top")])]})])],"derivedFrom":makeQuery(id+"F1.opExtrude","SWEPT_FACE",FACE,{"disambiguationData":[OSD([sQuery(id+"F0.wireOp",EDGE,"E0.bottom")])]})});
            var Q19;
            Q19=makeQuery(id+"F3.boolean.opBoolean","SPLIT",FACE,{"disambiguationData":[TD([makeQuery(id+"F3.opExtrude","SWEPT_FACE",FACE,{"disambiguationData":[OSD([sQuery(id+"F2.wireOp",EDGE,"E54")])]})])],"derivedFrom":makeQuery(id+"F1.opExtrude","SWEPT_FACE",FACE,{"disambiguationData":[OSD([sQuery(id+"F0.wireOp",EDGE,"E0.bottom")])]})});
            var Q20;
            Q20=makeQuery(id+"F3.boolean.opBoolean","SPLIT",FACE,{"disambiguationData":[TD([makeQuery(id+"F3.opExtrude","SWEPT_FACE",FACE,{"disambiguationData":[OSD([sQuery(id+"F2.wireOp",EDGE,"E57")])]})])],"derivedFrom":makeQuery(id+"F1.opExtrude","SWEPT_FACE",FACE,{"disambiguationData":[OSD([sQuery(id+"F0.wireOp",EDGE,"E0.bottom")])]})});
            var Q21;
            Q21=makeQuery(id+"F3.boolean.opBoolean","SPLIT",FACE,{"disambiguationData":[TD([makeQuery(id+"F3.opExtrude","SWEPT_FACE",FACE,{"disambiguationData":[OSD([sQuery(id+"F2.wireOp",EDGE,"E60")])]})])],"derivedFrom":makeQuery(id+"F1.opExtrude","SWEPT_FACE",FACE,{"disambiguationData":[OSD([sQuery(id+"F0.wireOp",EDGE,"E0.bottom")])]})});
            var Q22;
            Q22=makeQuery(id+"F3.boolean.opBoolean","SPLIT",FACE,{"disambiguationData":[TD([makeQuery(id+"F3.opExtrude","SWEPT_FACE",FACE,{"disambiguationData":[OSD([sQuery(id+"F2.wireOp",EDGE,"E63")])]})])],"derivedFrom":makeQuery(id+"F1.opExtrude","SWEPT_FACE",FACE,{"disambiguationData":[OSD([sQuery(id+"F0.wireOp",EDGE,"E0.bottom")])]})});
            var Q23;
            Q23=makeQuery(id+"F3.boolean.opBoolean","SPLIT",FACE,{"disambiguationData":[TD([makeQuery(id+"F3.opExtrude","SWEPT_FACE",FACE,{"disambiguationData":[OSD([sQuery(id+"F2.wireOp",EDGE,"E92")])]})])],"derivedFrom":makeQuery(id+"F1.opExtrude","SWEPT_FACE",FACE,{"disambiguationData":[OSD([sQuery(id+"F0.wireOp",EDGE,"E0.bottom")])]})});
            var Q24;
            Q24=makeQuery(id+"F3.boolean.opBoolean","SPLIT",FACE,{"disambiguationData":[TD([makeQuery(id+"F3.opExtrude","SWEPT_FACE",FACE,{"disambiguationData":[OSD([sQuery(id+"F2.wireOp",EDGE,"E89")])]})])],"derivedFrom":makeQuery(id+"F1.opExtrude","SWEPT_FACE",FACE,{"disambiguationData":[OSD([sQuery(id+"F0.wireOp",EDGE,"E0.bottom")])]})});
            var Q25;
            Q25=makeQuery(id+"F3.boolean.opBoolean","SPLIT",FACE,{"disambiguationData":[TD([makeQuery(id+"F3.opExtrude","SWEPT_FACE",FACE,{"disambiguationData":[OSD([sQuery(id+"F2.wireOp",EDGE,"E86")])]})])],"derivedFrom":makeQuery(id+"F1.opExtrude","SWEPT_FACE",FACE,{"disambiguationData":[OSD([sQuery(id+"F0.wireOp",EDGE,"E0.bottom")])]})});
            var Q26;
            Q26=makeQuery(id+"F3.boolean.opBoolean","SPLIT",FACE,{"disambiguationData":[TD([makeQuery(id+"F3.opExtrude","SWEPT_FACE",FACE,{"disambiguationData":[OSD([sQuery(id+"F2.wireOp",EDGE,"E83")])]})])],"derivedFrom":makeQuery(id+"F1.opExtrude","SWEPT_FACE",FACE,{"disambiguationData":[OSD([sQuery(id+"F0.wireOp",EDGE,"E0.bottom")])]})});
            var Q27;
            Q27=makeQuery(id+"F3.boolean.opBoolean","SPLIT",FACE,{"disambiguationData":[TD([makeQuery(id+"F3.opExtrude","SWEPT_FACE",FACE,{"disambiguationData":[OSD([sQuery(id+"F2.wireOp",EDGE,"E81")])]})])],"derivedFrom":makeQuery(id+"F1.opExtrude","SWEPT_FACE",FACE,{"disambiguationData":[OSD([sQuery(id+"F0.wireOp",EDGE,"E0.bottom")])]})});
            var Q28;
            Q28=makeQuery(id+"F3.boolean.opBoolean","SPLIT",FACE,{"disambiguationData":[TD([makeQuery(id+"F3.opExtrude","SWEPT_FACE",FACE,{"disambiguationData":[OSD([sQuery(id+"F2.wireOp",EDGE,"E79")])]})])],"derivedFrom":makeQuery(id+"F1.opExtrude","SWEPT_FACE",FACE,{"disambiguationData":[OSD([sQuery(id+"F0.wireOp",EDGE,"E0.bottom")])]})});
            var Q29;
            Q29=makeQuery(id+"F3.boolean.opBoolean","COPY",EDGE,{"derivedFrom":makeQuery(id+"F3.opExtrude","SWEPT_EDGE",EDGE,{"disambiguationData":[OSD([sQuery(id+"F0.wireOp",EDGE,"E0.bottom"),sQuery(id+"F0.wireOp",EDGE,"E0.left"),sQuery(id+"F2.wireOp",EDGE,"E97"),sQuery(id+"F2.wireOp",EDGE,"E98")])]})});
            var Q30;
            Q30=makeQuery(id+"F3.boolean.opBoolean","SPLIT",FACE,{"disambiguationData":[TD([makeQuery(id+"F3.opExtrude","SWEPT_FACE",FACE,{"disambiguationData":[OSD([sQuery(id+"F2.wireOp",EDGE,"E97")])]})])],"derivedFrom":makeQuery(id+"F1.opExtrude","SWEPT_FACE",FACE,{"disambiguationData":[OSD([sQuery(id+"F0.wireOp",EDGE,"E0.bottom")])]})});
            var Q31;
            Q31=makeQuery(id+"F3.boolean.opBoolean","SPLIT",FACE,{"disambiguationData":[TD([makeQuery(id+"F3.opExtrude","SWEPT_FACE",FACE,{"disambiguationData":[OSD([sQuery(id+"F2.wireOp",EDGE,"E101")])]})])],"derivedFrom":makeQuery(id+"F1.opExtrude","SWEPT_FACE",FACE,{"disambiguationData":[OSD([sQuery(id+"F0.wireOp",EDGE,"E0.bottom")])]})});
            var Q32;
            Q32=makeQuery(id+"F3.boolean.opBoolean","SPLIT",FACE,{"disambiguationData":[TD([makeQuery(id+"F3.opExtrude","SWEPT_FACE",FACE,{"disambiguationData":[OSD([sQuery(id+"F2.wireOp",EDGE,"E105")])]})])],"derivedFrom":makeQuery(id+"F1.opExtrude","SWEPT_FACE",FACE,{"disambiguationData":[OSD([sQuery(id+"F0.wireOp",EDGE,"E0.bottom")])]})});
            var Q33;
            Q33=makeQuery(id+"F3.boolean.opBoolean","SPLIT",FACE,{"disambiguationData":[TD([makeQuery(id+"F3.opExtrude","SWEPT_FACE",FACE,{"disambiguationData":[OSD([sQuery(id+"F2.wireOp",EDGE,"E64.MirrorCS")])]})])],"derivedFrom":makeQuery(id+"F1.opExtrude","SWEPT_FACE",FACE,{"disambiguationData":[OSD([sQuery(id+"F0.wireOp",EDGE,"E0.bottom")])]})});
            var Q34;
            Q34=makeQuery(id+"F3.boolean.opBoolean","SPLIT",FACE,{"disambiguationData":[TD([makeQuery(id+"F3.opExtrude","SWEPT_FACE",FACE,{"disambiguationData":[OSD([sQuery(id+"F2.wireOp",EDGE,"E111")])]})])],"derivedFrom":makeQuery(id+"F1.opExtrude","SWEPT_FACE",FACE,{"disambiguationData":[OSD([sQuery(id+"F0.wireOp",EDGE,"E0.bottom")])]})});
            var Q35;
            Q35=makeQuery(id+"F3.boolean.opBoolean","SPLIT",FACE,{"disambiguationData":[TD([makeQuery(id+"F3.opExtrude","SWEPT_FACE",FACE,{"disambiguationData":[OSD([sQuery(id+"F2.wireOp",EDGE,"E115")])]})])],"derivedFrom":makeQuery(id+"F1.opExtrude","SWEPT_FACE",FACE,{"disambiguationData":[OSD([sQuery(id+"F0.wireOp",EDGE,"E0.bottom")])]})});
            var Q36;
            Q36=makeQuery(id+"F3.boolean.opBoolean","SPLIT",FACE,{"disambiguationData":[TD([makeQuery(id+"F3.opExtrude","SWEPT_FACE",FACE,{"disambiguationData":[OSD([sQuery(id+"F2.wireOp",EDGE,"E119")])]})])],"derivedFrom":makeQuery(id+"F1.opExtrude","SWEPT_FACE",FACE,{"disambiguationData":[OSD([sQuery(id+"F0.wireOp",EDGE,"E0.bottom")])]})});
            var Q37;
            Q37=makeQuery(id+"F3.boolean.opBoolean","SPLIT",FACE,{"disambiguationData":[TD([makeQuery(id+"F3.opExtrude","SWEPT_FACE",FACE,{"disambiguationData":[OSD([sQuery(id+"F2.wireOp",EDGE,"E123")])]})])],"derivedFrom":makeQuery(id+"F1.opExtrude","SWEPT_FACE",FACE,{"disambiguationData":[OSD([sQuery(id+"F0.wireOp",EDGE,"E0.bottom")])]})});
            var Q38;
            Q38=makeQuery(id+"F3.boolean.opBoolean","SPLIT",FACE,{"disambiguationData":[TD([makeQuery(id+"F3.opExtrude","SWEPT_FACE",FACE,{"disambiguationData":[OSD([sQuery(id+"F2.wireOp",EDGE,"E127")])]})])],"derivedFrom":makeQuery(id+"F1.opExtrude","SWEPT_FACE",FACE,{"disambiguationData":[OSD([sQuery(id+"F0.wireOp",EDGE,"E0.bottom")])]})});
            var Q39;
            Q39=makeQuery(id+"F3.boolean.opBoolean","SPLIT",FACE,{"disambiguationData":[TD([makeQuery(id+"F3.opExtrude","SWEPT_FACE",FACE,{"disambiguationData":[OSD([sQuery(id+"F2.wireOp",EDGE,"E131")])]})])],"derivedFrom":makeQuery(id+"F1.opExtrude","SWEPT_FACE",FACE,{"disambiguationData":[OSD([sQuery(id+"F0.wireOp",EDGE,"E0.bottom")])]})});
            var Q40;
            Q40=makeQuery(id+"F3.boolean.opBoolean","SPLIT",FACE,{"disambiguationData":[TD([makeQuery(id+"F3.opExtrude","SWEPT_FACE",FACE,{"disambiguationData":[OSD([sQuery(id+"F2.wireOp",EDGE,"E135")])]})])],"derivedFrom":makeQuery(id+"F1.opExtrude","SWEPT_FACE",FACE,{"disambiguationData":[OSD([sQuery(id+"F0.wireOp",EDGE,"E0.bottom")])]})});
            var Q41;
            Q41=makeQuery(id+"F3.boolean.opBoolean","SPLIT",FACE,{"disambiguationData":[TD([makeQuery(id+"F3.opExtrude","SWEPT_FACE",FACE,{"disambiguationData":[OSD([sQuery(id+"F2.wireOp",EDGE,"E139")])]})])],"derivedFrom":makeQuery(id+"F1.opExtrude","SWEPT_FACE",FACE,{"disambiguationData":[OSD([sQuery(id+"F0.wireOp",EDGE,"E0.bottom")])]})});
            var Q42;
            Q42=makeQuery(id+"F3.boolean.opBoolean","SPLIT",FACE,{"disambiguationData":[TD([makeQuery(id+"F3.opExtrude","SWEPT_FACE",FACE,{"disambiguationData":[OSD([sQuery(id+"F2.wireOp",EDGE,"E143")])]})])],"derivedFrom":makeQuery(id+"F1.opExtrude","SWEPT_FACE",FACE,{"disambiguationData":[OSD([sQuery(id+"F0.wireOp",EDGE,"E0.bottom")])]})});
            var Q43;
            Q43=makeQuery(id+"F3.boolean.opBoolean","SPLIT",FACE,{"disambiguationData":[TD([makeQuery(id+"F3.opExtrude","SWEPT_FACE",FACE,{"disambiguationData":[OSD([sQuery(id+"F2.wireOp",EDGE,"E147")])]})])],"derivedFrom":makeQuery(id+"F1.opExtrude","SWEPT_FACE",FACE,{"disambiguationData":[OSD([sQuery(id+"F0.wireOp",EDGE,"E0.bottom")])]})});
            chamfer(context, id + "F6", {"entities" : qUnion([Q0, Q1, Q2, Q3, Q4, Q5, Q6, Q7, Q8, Q9, Q10, Q11, Q12, Q13, Q14, Q15, Q16, Q17, Q18, Q19, Q20, Q21, Q22, Q23, Q24, Q25, Q26, Q27, Q28, Q29, Q30, Q31, Q32, Q33, Q34, Q35, Q36, Q37, Q38, Q39, Q40, Q41, Q42, Q43]), "width" : 0.5 * mm, "tangentPropagation" : true});
        }
        {
            var Q0;
            {var subQ2=sQuery(id+"F0.wireOp",EDGE,"E0.bottom");Q0=makeQuery(id+"F3.boolean.opBoolean","SPLIT",FACE,{"disambiguationData":[TD([makeQuery(id+"F3.opExtrude","SWEPT_FACE",FACE,{"disambiguationData":[OSD([sQuery(id+"F2.wireOp",EDGE,"E151")])]})])],"derivedFrom":makeQuery(id+"F1.opExtrude","SWEPT_FACE",FACE,{"disambiguationData":[OSD([subQ2])]})});}
            var sketch = newSketch(context, id + "F7", { "sketchPlane" : qUnion([Q0])});
            skLineSegment(sketch, "E152.bottom", {"start": v(0, 3.3) * mm, "end": v(40.64, 3.3) * mm});
            skLineSegment(sketch, "E152.top", {"start": v(0, 0.75) * mm, "end": v(40.64, 0.75) * mm});
            skLineSegment(sketch, "E152.left", {"start": v(0, 3.3) * mm, "end": v(0, 0.75) * mm});
            skLineSegment(sketch, "E152.right", {"start": v(40.64, 3.3) * mm, "end": v(40.64, 0.75) * mm});
            skSolve(sketch);
        }
        {
            var Q0;
            {var subQ0=sQuery(id+"F7.wireOp",EDGE,"E152.top");Q0=makeQuery(id+"F7.imprint","IMPRINT",FACE,{"disambiguationData":[TD([[makeQuery(id+"F7.imprint","IMPRINT",EDGE,{"derivedFrom":subQ0}),-1.0]])]});}
            extrude(context, id + "F8", {"entities" : qUnion([Q0]), "operationType" : NewBodyOperationType.REMOVE, "endBound" : BoundingType.THROUGH_ALL, "oppositeDirection" : true, "depth" : 25.4 * mm, "offsetDistance" : 25.4 * mm});
        }
        {
            var Q0;
            {var subQ2=sQuery(id+"F0.wireOp",EDGE,"E0.bottom");Q0=makeQuery(id+"F3.boolean.opBoolean","SPLIT",FACE,{"disambiguationData":[TD([makeQuery(id+"F3.opExtrude","SWEPT_FACE",FACE,{"disambiguationData":[OSD([sQuery(id+"F2.wireOp",EDGE,"E151")])]})])],"derivedFrom":makeQuery(id+"F1.opExtrude","SWEPT_FACE",FACE,{"disambiguationData":[OSD([subQ2])]})});}
            chamfer(context, id + "F9", {"entities" : qUnion([Q0]), "width" : 0.5 * mm, "tangentPropagation" : true});
        }
        {
            var Q0;
            {var subQ0=sQuery(id+"F2.wireOp",EDGE,"E5");Q0=makeQuery(id+"F6.opChamfer","BLEND_EDGE",EDGE,{"blendedFrom":[makeQuery(id+"F3.boolean.opBoolean","COPY",EDGE,{"derivedFrom":makeQuery(id+"F3.opExtrude","SWEPT_EDGE",EDGE,{"disambiguationData":[OSD([sQuery(id+"F2.wireOp",EDGE,"E3"),subQ0])]})}),makeQuery(id+"F3.boolean.opBoolean","COPY",FACE,{"derivedFrom":makeQuery(id+"F3.opExtrude","SWEPT_FACE",FACE,{"disambiguationData":[OSD([subQ0])]})})],"blendedInto":[makeQuery(id+"F3.boolean.opBoolean","COPY",FACE,{"derivedFrom":makeQuery(id+"F3.opExtrude","SWEPT_FACE",FACE,{"disambiguationData":[OSD([subQ0])]})})]});}
            var Q1;
            {var subQ0=sQuery(id+"F2.wireOp",EDGE,"E4");Q1=makeQuery(id+"F6.opChamfer","BLEND_EDGE",EDGE,{"blendedFrom":[makeQuery(id+"F3.boolean.opBoolean","COPY",EDGE,{"derivedFrom":makeQuery(id+"F3.opExtrude","SWEPT_EDGE",EDGE,{"disambiguationData":[OSD([sQuery(id+"F2.wireOp",EDGE,"E3"),subQ0,sQuery(id+"F2.wireOp",EDGE,"E6")])]})}),makeQuery(id+"F3.boolean.opBoolean","COPY",FACE,{"derivedFrom":makeQuery(id+"F3.opExtrude","SWEPT_FACE",FACE,{"disambiguationData":[OSD([subQ0])]})})],"blendedInto":[makeQuery(id+"F3.boolean.opBoolean","COPY",FACE,{"derivedFrom":makeQuery(id+"F3.opExtrude","SWEPT_FACE",FACE,{"disambiguationData":[OSD([subQ0])]})})]});}
            var Q2;
            {var subQ0=sQuery(id+"F2.wireOp",EDGE,"E10");Q2=makeQuery(id+"F6.opChamfer","BLEND_EDGE",EDGE,{"blendedFrom":[makeQuery(id+"F3.boolean.opBoolean","COPY",EDGE,{"derivedFrom":makeQuery(id+"F3.opExtrude","SWEPT_EDGE",EDGE,{"disambiguationData":[OSD([sQuery(id+"F2.wireOp",EDGE,"E6"),subQ0])]})}),makeQuery(id+"F3.boolean.opBoolean","COPY",FACE,{"derivedFrom":makeQuery(id+"F3.opExtrude","SWEPT_FACE",FACE,{"disambiguationData":[OSD([subQ0])]})})],"blendedInto":[makeQuery(id+"F3.boolean.opBoolean","COPY",FACE,{"derivedFrom":makeQuery(id+"F3.opExtrude","SWEPT_FACE",FACE,{"disambiguationData":[OSD([subQ0])]})})]});}
            var Q3;
            {var subQ0=sQuery(id+"F2.wireOp",EDGE,"E8");Q3=makeQuery(id+"F6.opChamfer","BLEND_EDGE",EDGE,{"blendedFrom":[makeQuery(id+"F3.boolean.opBoolean","COPY",EDGE,{"derivedFrom":makeQuery(id+"F3.opExtrude","SWEPT_EDGE",EDGE,{"disambiguationData":[OSD([sQuery(id+"F2.wireOp",EDGE,"E6"),subQ0])]})}),makeQuery(id+"F3.boolean.opBoolean","COPY",FACE,{"derivedFrom":makeQuery(id+"F3.opExtrude","SWEPT_FACE",FACE,{"disambiguationData":[OSD([subQ0])]})})],"blendedInto":[makeQuery(id+"F3.boolean.opBoolean","COPY",FACE,{"derivedFrom":makeQuery(id+"F3.opExtrude","SWEPT_FACE",FACE,{"disambiguationData":[OSD([subQ0])]})})]});}
            var Q4;
            {var subQ0=sQuery(id+"F2.wireOp",EDGE,"E12");Q4=makeQuery(id+"F6.opChamfer","BLEND_EDGE",EDGE,{"blendedFrom":[makeQuery(id+"F3.boolean.opBoolean","COPY",EDGE,{"derivedFrom":makeQuery(id+"F3.opExtrude","SWEPT_EDGE",EDGE,{"disambiguationData":[OSD([sQuery(id+"F2.wireOp",EDGE,"E6"),sQuery(id+"F2.wireOp",EDGE,"E11"),subQ0])]})}),makeQuery(id+"F3.boolean.opBoolean","COPY",FACE,{"derivedFrom":makeQuery(id+"F3.opExtrude","SWEPT_FACE",FACE,{"disambiguationData":[OSD([subQ0])]})})],"blendedInto":[makeQuery(id+"F3.boolean.opBoolean","COPY",FACE,{"derivedFrom":makeQuery(id+"F3.opExtrude","SWEPT_FACE",FACE,{"disambiguationData":[OSD([subQ0])]})})]});}
            var Q5;
            {var subQ0=sQuery(id+"F2.wireOp",EDGE,"E7");Q5=makeQuery(id+"F6.opChamfer","BLEND_EDGE",EDGE,{"blendedFrom":[makeQuery(id+"F3.boolean.opBoolean","COPY",EDGE,{"derivedFrom":makeQuery(id+"F3.opExtrude","SWEPT_EDGE",EDGE,{"disambiguationData":[OSD([sQuery(id+"F0.wireOp",EDGE,"E0.bottom"),sQuery(id+"F0.wireOp",EDGE,"E0.left"),subQ0,sQuery(id+"F2.wireOp",EDGE,"E11")])]})}),makeQuery(id+"F3.boolean.opBoolean","COPY",FACE,{"derivedFrom":makeQuery(id+"F3.opExtrude","SWEPT_FACE",FACE,{"disambiguationData":[OSD([subQ0])]})})],"blendedInto":[makeQuery(id+"F3.boolean.opBoolean","COPY",FACE,{"derivedFrom":makeQuery(id+"F3.opExtrude","SWEPT_FACE",FACE,{"disambiguationData":[OSD([subQ0])]})})]});}
            var Q6;
            {var subQ0=sQuery(id+"F2.wireOp",EDGE,"E16");Q6=makeQuery(id+"F6.opChamfer","BLEND_EDGE",EDGE,{"blendedFrom":[makeQuery(id+"F3.boolean.opBoolean","COPY",EDGE,{"derivedFrom":makeQuery(id+"F3.opExtrude","SWEPT_EDGE",EDGE,{"disambiguationData":[OSD([sQuery(id+"F0.wireOp",EDGE,"E0.bottom"),sQuery(id+"F0.wireOp",EDGE,"E0.left"),sQuery(id+"F2.wireOp",EDGE,"E15"),subQ0])]})}),makeQuery(id+"F3.boolean.opBoolean","COPY",FACE,{"derivedFrom":makeQuery(id+"F3.opExtrude","SWEPT_FACE",FACE,{"disambiguationData":[OSD([subQ0])]})})],"blendedInto":[makeQuery(id+"F3.boolean.opBoolean","COPY",FACE,{"derivedFrom":makeQuery(id+"F3.opExtrude","SWEPT_FACE",FACE,{"disambiguationData":[OSD([subQ0])]})})]});}
            var Q7;
            {var subQ0=sQuery(id+"F2.wireOp",EDGE,"E14");Q7=makeQuery(id+"F6.opChamfer","BLEND_EDGE",EDGE,{"blendedFrom":[makeQuery(id+"F3.boolean.opBoolean","COPY",EDGE,{"derivedFrom":makeQuery(id+"F3.opExtrude","SWEPT_EDGE",EDGE,{"disambiguationData":[OSD([sQuery(id+"F0.wireOp",EDGE,"E0.bottom"),sQuery(id+"F0.wireOp",EDGE,"E0.left"),subQ0,sQuery(id+"F2.wireOp",EDGE,"E15")])]})}),makeQuery(id+"F3.boolean.opBoolean","COPY",FACE,{"derivedFrom":makeQuery(id+"F3.opExtrude","SWEPT_FACE",FACE,{"disambiguationData":[OSD([subQ0])]})})],"blendedInto":[makeQuery(id+"F3.boolean.opBoolean","COPY",FACE,{"derivedFrom":makeQuery(id+"F3.opExtrude","SWEPT_FACE",FACE,{"disambiguationData":[OSD([subQ0])]})})]});}
            var Q8;
            {var subQ0=sQuery(id+"F2.wireOp",EDGE,"E20");Q8=makeQuery(id+"F6.opChamfer","BLEND_EDGE",EDGE,{"blendedFrom":[makeQuery(id+"F3.boolean.opBoolean","COPY",EDGE,{"derivedFrom":makeQuery(id+"F3.opExtrude","SWEPT_EDGE",EDGE,{"disambiguationData":[OSD([sQuery(id+"F0.wireOp",EDGE,"E0.bottom"),sQuery(id+"F0.wireOp",EDGE,"E0.left"),sQuery(id+"F2.wireOp",EDGE,"E19"),subQ0])]})}),makeQuery(id+"F3.boolean.opBoolean","COPY",FACE,{"derivedFrom":makeQuery(id+"F3.opExtrude","SWEPT_FACE",FACE,{"disambiguationData":[OSD([subQ0])]})})],"blendedInto":[makeQuery(id+"F3.boolean.opBoolean","COPY",FACE,{"derivedFrom":makeQuery(id+"F3.opExtrude","SWEPT_FACE",FACE,{"disambiguationData":[OSD([subQ0])]})})]});}
            var Q9;
            {var subQ0=sQuery(id+"F2.wireOp",EDGE,"E18");Q9=makeQuery(id+"F6.opChamfer","BLEND_EDGE",EDGE,{"blendedFrom":[makeQuery(id+"F3.boolean.opBoolean","COPY",EDGE,{"derivedFrom":makeQuery(id+"F3.opExtrude","SWEPT_EDGE",EDGE,{"disambiguationData":[OSD([sQuery(id+"F0.wireOp",EDGE,"E0.bottom"),sQuery(id+"F0.wireOp",EDGE,"E0.left"),subQ0,sQuery(id+"F2.wireOp",EDGE,"E19")])]})}),makeQuery(id+"F3.boolean.opBoolean","COPY",FACE,{"derivedFrom":makeQuery(id+"F3.opExtrude","SWEPT_FACE",FACE,{"disambiguationData":[OSD([subQ0])]})})],"blendedInto":[makeQuery(id+"F3.boolean.opBoolean","COPY",FACE,{"derivedFrom":makeQuery(id+"F3.opExtrude","SWEPT_FACE",FACE,{"disambiguationData":[OSD([subQ0])]})})]});}
            var Q10;
            {var subQ0=sQuery(id+"F2.wireOp",EDGE,"E24");Q10=makeQuery(id+"F6.opChamfer","BLEND_EDGE",EDGE,{"blendedFrom":[makeQuery(id+"F3.boolean.opBoolean","COPY",EDGE,{"derivedFrom":makeQuery(id+"F3.opExtrude","SWEPT_EDGE",EDGE,{"disambiguationData":[OSD([sQuery(id+"F0.wireOp",EDGE,"E0.bottom"),sQuery(id+"F0.wireOp",EDGE,"E0.left"),sQuery(id+"F2.wireOp",EDGE,"E23"),subQ0])]})}),makeQuery(id+"F3.boolean.opBoolean","COPY",FACE,{"derivedFrom":makeQuery(id+"F3.opExtrude","SWEPT_FACE",FACE,{"disambiguationData":[OSD([subQ0])]})})],"blendedInto":[makeQuery(id+"F3.boolean.opBoolean","COPY",FACE,{"derivedFrom":makeQuery(id+"F3.opExtrude","SWEPT_FACE",FACE,{"disambiguationData":[OSD([subQ0])]})})]});}
            var Q11;
            {var subQ0=sQuery(id+"F2.wireOp",EDGE,"E22");Q11=makeQuery(id+"F6.opChamfer","BLEND_EDGE",EDGE,{"blendedFrom":[makeQuery(id+"F3.boolean.opBoolean","COPY",EDGE,{"derivedFrom":makeQuery(id+"F3.opExtrude","SWEPT_EDGE",EDGE,{"disambiguationData":[OSD([sQuery(id+"F0.wireOp",EDGE,"E0.bottom"),sQuery(id+"F0.wireOp",EDGE,"E0.left"),subQ0,sQuery(id+"F2.wireOp",EDGE,"E23")])]})}),makeQuery(id+"F3.boolean.opBoolean","COPY",FACE,{"derivedFrom":makeQuery(id+"F3.opExtrude","SWEPT_FACE",FACE,{"disambiguationData":[OSD([subQ0])]})})],"blendedInto":[makeQuery(id+"F3.boolean.opBoolean","COPY",FACE,{"derivedFrom":makeQuery(id+"F3.opExtrude","SWEPT_FACE",FACE,{"disambiguationData":[OSD([subQ0])]})})]});}
            var Q12;
            {var subQ0=sQuery(id+"F2.wireOp",EDGE,"E29");Q12=makeQuery(id+"F6.opChamfer","BLEND_EDGE",EDGE,{"blendedFrom":[makeQuery(id+"F3.boolean.opBoolean","COPY",EDGE,{"derivedFrom":makeQuery(id+"F3.opExtrude","SWEPT_EDGE",EDGE,{"disambiguationData":[OSD([sQuery(id+"F0.wireOp",EDGE,"E0.bottom"),sQuery(id+"F0.wireOp",EDGE,"E0.left"),sQuery(id+"F2.wireOp",EDGE,"E28"),subQ0])]})}),makeQuery(id+"F3.boolean.opBoolean","COPY",FACE,{"derivedFrom":makeQuery(id+"F3.opExtrude","SWEPT_FACE",FACE,{"disambiguationData":[OSD([subQ0])]})})],"blendedInto":[makeQuery(id+"F3.boolean.opBoolean","COPY",FACE,{"derivedFrom":makeQuery(id+"F3.opExtrude","SWEPT_FACE",FACE,{"disambiguationData":[OSD([subQ0])]})})]});}
            var Q13;
            {var subQ0=sQuery(id+"F2.wireOp",EDGE,"E26");Q13=makeQuery(id+"F6.opChamfer","BLEND_EDGE",EDGE,{"blendedFrom":[makeQuery(id+"F3.boolean.opBoolean","COPY",EDGE,{"derivedFrom":makeQuery(id+"F3.opExtrude","SWEPT_EDGE",EDGE,{"disambiguationData":[OSD([sQuery(id+"F0.wireOp",EDGE,"E0.bottom"),sQuery(id+"F0.wireOp",EDGE,"E0.left"),subQ0,sQuery(id+"F2.wireOp",EDGE,"E28")])]})}),makeQuery(id+"F3.boolean.opBoolean","COPY",FACE,{"derivedFrom":makeQuery(id+"F3.opExtrude","SWEPT_FACE",FACE,{"disambiguationData":[OSD([subQ0])]})})],"blendedInto":[makeQuery(id+"F3.boolean.opBoolean","COPY",FACE,{"derivedFrom":makeQuery(id+"F3.opExtrude","SWEPT_FACE",FACE,{"disambiguationData":[OSD([subQ0])]})})]});}
            var Q14;
            {var subQ0=sQuery(id+"F2.wireOp",EDGE,"E33");Q14=makeQuery(id+"F6.opChamfer","BLEND_EDGE",EDGE,{"blendedFrom":[makeQuery(id+"F3.boolean.opBoolean","COPY",EDGE,{"derivedFrom":makeQuery(id+"F3.opExtrude","SWEPT_EDGE",EDGE,{"disambiguationData":[OSD([sQuery(id+"F0.wireOp",EDGE,"E0.bottom"),sQuery(id+"F0.wireOp",EDGE,"E0.left"),sQuery(id+"F2.wireOp",EDGE,"E32"),subQ0])]})}),makeQuery(id+"F3.boolean.opBoolean","COPY",FACE,{"derivedFrom":makeQuery(id+"F3.opExtrude","SWEPT_FACE",FACE,{"disambiguationData":[OSD([subQ0])]})})],"blendedInto":[makeQuery(id+"F3.boolean.opBoolean","COPY",FACE,{"derivedFrom":makeQuery(id+"F3.opExtrude","SWEPT_FACE",FACE,{"disambiguationData":[OSD([subQ0])]})})]});}
            var Q15;
            {var subQ0=sQuery(id+"F2.wireOp",EDGE,"E31");Q15=makeQuery(id+"F6.opChamfer","BLEND_EDGE",EDGE,{"blendedFrom":[makeQuery(id+"F3.boolean.opBoolean","COPY",EDGE,{"derivedFrom":makeQuery(id+"F3.opExtrude","SWEPT_EDGE",EDGE,{"disambiguationData":[OSD([subQ0,sQuery(id+"F2.wireOp",EDGE,"E32"),sQuery(id+"F2.wireOp",EDGE,"E35.MirrorCS")])]})}),makeQuery(id+"F3.boolean.opBoolean","COPY",FACE,{"derivedFrom":makeQuery(id+"F3.opExtrude","SWEPT_FACE",FACE,{"disambiguationData":[OSD([subQ0])]})})],"blendedInto":[makeQuery(id+"F3.boolean.opBoolean","COPY",FACE,{"derivedFrom":makeQuery(id+"F3.opExtrude","SWEPT_FACE",FACE,{"disambiguationData":[OSD([subQ0])]})})]});}
            var Q16;
            {var subQ0=sQuery(id+"F2.wireOp",EDGE,"E38");Q16=makeQuery(id+"F6.opChamfer","BLEND_EDGE",EDGE,{"blendedFrom":[makeQuery(id+"F3.boolean.opBoolean","COPY",EDGE,{"derivedFrom":makeQuery(id+"F3.opExtrude","SWEPT_EDGE",EDGE,{"disambiguationData":[OSD([sQuery(id+"F0.wireOp",EDGE,"E0.bottom"),sQuery(id+"F0.wireOp",EDGE,"E0.left"),sQuery(id+"F2.wireOp",EDGE,"E35.MirrorCS"),subQ0])]})}),makeQuery(id+"F3.boolean.opBoolean","COPY",FACE,{"derivedFrom":makeQuery(id+"F3.opExtrude","SWEPT_FACE",FACE,{"disambiguationData":[OSD([subQ0])]})})],"blendedInto":[makeQuery(id+"F3.boolean.opBoolean","COPY",FACE,{"derivedFrom":makeQuery(id+"F3.opExtrude","SWEPT_FACE",FACE,{"disambiguationData":[OSD([subQ0])]})})]});}
            var Q17;
            {var subQ0=sQuery(id+"F2.wireOp",EDGE,"E37.MirrorCS");Q17=makeQuery(id+"F6.opChamfer","BLEND_EDGE",EDGE,{"blendedFrom":[makeQuery(id+"F3.boolean.opBoolean","COPY",EDGE,{"derivedFrom":makeQuery(id+"F3.opExtrude","SWEPT_EDGE",EDGE,{"disambiguationData":[OSD([sQuery(id+"F0.wireOp",EDGE,"E0.bottom"),sQuery(id+"F0.wireOp",EDGE,"E0.left"),subQ0])]})}),makeQuery(id+"F3.boolean.opBoolean","COPY",FACE,{"derivedFrom":makeQuery(id+"F3.opExtrude","SWEPT_FACE",FACE,{"disambiguationData":[OSD([subQ0])]})})],"blendedInto":[makeQuery(id+"F3.boolean.opBoolean","COPY",FACE,{"derivedFrom":makeQuery(id+"F3.opExtrude","SWEPT_FACE",FACE,{"disambiguationData":[OSD([subQ0])]})})]});}
            var Q18;
            {var subQ0=sQuery(id+"F2.wireOp",EDGE,"E40.top");Q18=makeQuery(id+"F6.opChamfer","BLEND_EDGE",EDGE,{"blendedFrom":[makeQuery(id+"F3.boolean.opBoolean","COPY",EDGE,{"derivedFrom":makeQuery(id+"F3.opExtrude","SWEPT_EDGE",EDGE,{"disambiguationData":[OSD([sQuery(id+"F2.wireOp",EDGE,"E40.right"),subQ0,sQuery(id+"F2.wireOp",EDGE,"E41.right")])]})}),makeQuery(id+"F3.boolean.opBoolean","COPY",FACE,{"derivedFrom":makeQuery(id+"F3.opExtrude","SWEPT_FACE",FACE,{"disambiguationData":[OSD([subQ0])]})})],"blendedInto":[makeQuery(id+"F3.boolean.opBoolean","COPY",FACE,{"derivedFrom":makeQuery(id+"F3.opExtrude","SWEPT_FACE",FACE,{"disambiguationData":[OSD([subQ0])]})})]});}
            var Q19;
            {var subQ0=sQuery(id+"F2.wireOp",EDGE,"E39.top");Q19=makeQuery(id+"F6.opChamfer","BLEND_EDGE",EDGE,{"blendedFrom":[makeQuery(id+"F3.boolean.opBoolean","COPY",EDGE,{"derivedFrom":makeQuery(id+"F3.opExtrude","SWEPT_EDGE",EDGE,{"disambiguationData":[OSD([sQuery(id+"F2.wireOp",EDGE,"E39.right"),subQ0,sQuery(id+"F2.wireOp",EDGE,"E40.right")])]})}),makeQuery(id+"F3.boolean.opBoolean","COPY",FACE,{"derivedFrom":makeQuery(id+"F3.opExtrude","SWEPT_FACE",FACE,{"disambiguationData":[OSD([subQ0])]})})],"blendedInto":[makeQuery(id+"F3.boolean.opBoolean","COPY",FACE,{"derivedFrom":makeQuery(id+"F3.opExtrude","SWEPT_FACE",FACE,{"disambiguationData":[OSD([subQ0])]})})]});}
            var Q20;
            {var subQ0=sQuery(id+"F2.wireOp",EDGE,"E41.top");Q20=makeQuery(id+"F6.opChamfer","BLEND_EDGE",EDGE,{"blendedFrom":[makeQuery(id+"F3.boolean.opBoolean","COPY",EDGE,{"derivedFrom":makeQuery(id+"F3.opExtrude","SWEPT_EDGE",EDGE,{"disambiguationData":[OSD([sQuery(id+"F2.wireOp",EDGE,"E41.right"),subQ0,sQuery(id+"F2.wireOp",EDGE,"E42.right")])]})}),makeQuery(id+"F3.boolean.opBoolean","COPY",FACE,{"derivedFrom":makeQuery(id+"F3.opExtrude","SWEPT_FACE",FACE,{"disambiguationData":[OSD([subQ0])]})})],"blendedInto":[makeQuery(id+"F3.boolean.opBoolean","COPY",FACE,{"derivedFrom":makeQuery(id+"F3.opExtrude","SWEPT_FACE",FACE,{"disambiguationData":[OSD([subQ0])]})})]});}
            var Q21;
            {var subQ0=sQuery(id+"F2.wireOp",EDGE,"E42.top");Q21=makeQuery(id+"F6.opChamfer","BLEND_EDGE",EDGE,{"blendedFrom":[makeQuery(id+"F3.boolean.opBoolean","COPY",EDGE,{"derivedFrom":makeQuery(id+"F3.opExtrude","SWEPT_EDGE",EDGE,{"disambiguationData":[OSD([sQuery(id+"F2.wireOp",EDGE,"E42.right"),subQ0,sQuery(id+"F2.wireOp",EDGE,"E43.right")])]})}),makeQuery(id+"F3.boolean.opBoolean","COPY",FACE,{"derivedFrom":makeQuery(id+"F3.opExtrude","SWEPT_FACE",FACE,{"disambiguationData":[OSD([subQ0])]})})],"blendedInto":[makeQuery(id+"F3.boolean.opBoolean","COPY",FACE,{"derivedFrom":makeQuery(id+"F3.opExtrude","SWEPT_FACE",FACE,{"disambiguationData":[OSD([subQ0])]})})]});}
            var Q22;
            {var subQ0=sQuery(id+"F2.wireOp",EDGE,"E43.top");Q22=makeQuery(id+"F6.opChamfer","BLEND_EDGE",EDGE,{"blendedFrom":[makeQuery(id+"F3.boolean.opBoolean","COPY",EDGE,{"derivedFrom":makeQuery(id+"F3.opExtrude","SWEPT_EDGE",EDGE,{"disambiguationData":[OSD([sQuery(id+"F0.wireOp",EDGE,"E0.bottom"),sQuery(id+"F0.wireOp",EDGE,"E0.left"),subQ0,sQuery(id+"F2.wireOp",EDGE,"E43.right")])]})}),makeQuery(id+"F3.boolean.opBoolean","COPY",FACE,{"derivedFrom":makeQuery(id+"F3.opExtrude","SWEPT_FACE",FACE,{"disambiguationData":[OSD([subQ0])]})})],"blendedInto":[makeQuery(id+"F3.boolean.opBoolean","COPY",FACE,{"derivedFrom":makeQuery(id+"F3.opExtrude","SWEPT_FACE",FACE,{"disambiguationData":[OSD([subQ0])]})})]});}
            var Q23;
            {var subQ0=sQuery(id+"F2.wireOp",EDGE,"E52");Q23=makeQuery(id+"F6.opChamfer","BLEND_EDGE",EDGE,{"blendedFrom":[makeQuery(id+"F3.boolean.opBoolean","COPY",EDGE,{"derivedFrom":makeQuery(id+"F3.opExtrude","SWEPT_EDGE",EDGE,{"disambiguationData":[OSD([sQuery(id+"F0.wireOp",EDGE,"E0.bottom"),sQuery(id+"F0.wireOp",EDGE,"E0.left"),subQ0,sQuery(id+"F2.wireOp",EDGE,"E53")])]})}),makeQuery(id+"F3.boolean.opBoolean","COPY",FACE,{"derivedFrom":makeQuery(id+"F3.opExtrude","SWEPT_FACE",FACE,{"disambiguationData":[OSD([subQ0])]})})],"blendedInto":[makeQuery(id+"F3.boolean.opBoolean","COPY",FACE,{"derivedFrom":makeQuery(id+"F3.opExtrude","SWEPT_FACE",FACE,{"disambiguationData":[OSD([subQ0])]})})]});}
            var Q24;
            {var subQ0=sQuery(id+"F2.wireOp",EDGE,"E54");Q24=makeQuery(id+"F6.opChamfer","BLEND_EDGE",EDGE,{"blendedFrom":[makeQuery(id+"F3.boolean.opBoolean","COPY",EDGE,{"derivedFrom":makeQuery(id+"F3.opExtrude","SWEPT_EDGE",EDGE,{"disambiguationData":[OSD([sQuery(id+"F0.wireOp",EDGE,"E0.bottom"),sQuery(id+"F0.wireOp",EDGE,"E0.left"),sQuery(id+"F2.wireOp",EDGE,"E53"),subQ0])]})}),makeQuery(id+"F3.boolean.opBoolean","COPY",FACE,{"derivedFrom":makeQuery(id+"F3.opExtrude","SWEPT_FACE",FACE,{"disambiguationData":[OSD([subQ0])]})})],"blendedInto":[makeQuery(id+"F3.boolean.opBoolean","COPY",FACE,{"derivedFrom":makeQuery(id+"F3.opExtrude","SWEPT_FACE",FACE,{"disambiguationData":[OSD([subQ0])]})})]});}
            var Q25;
            {var subQ0=sQuery(id+"F2.wireOp",EDGE,"E55");Q25=makeQuery(id+"F6.opChamfer","BLEND_EDGE",EDGE,{"blendedFrom":[makeQuery(id+"F3.boolean.opBoolean","COPY",EDGE,{"derivedFrom":makeQuery(id+"F3.opExtrude","SWEPT_EDGE",EDGE,{"disambiguationData":[OSD([sQuery(id+"F0.wireOp",EDGE,"E0.bottom"),sQuery(id+"F0.wireOp",EDGE,"E0.left"),subQ0,sQuery(id+"F2.wireOp",EDGE,"E56")])]})}),makeQuery(id+"F3.boolean.opBoolean","COPY",FACE,{"derivedFrom":makeQuery(id+"F3.opExtrude","SWEPT_FACE",FACE,{"disambiguationData":[OSD([subQ0])]})})],"blendedInto":[makeQuery(id+"F3.boolean.opBoolean","COPY",FACE,{"derivedFrom":makeQuery(id+"F3.opExtrude","SWEPT_FACE",FACE,{"disambiguationData":[OSD([subQ0])]})})]});}
            var Q26;
            {var subQ0=sQuery(id+"F2.wireOp",EDGE,"E57");Q26=makeQuery(id+"F6.opChamfer","BLEND_EDGE",EDGE,{"blendedFrom":[makeQuery(id+"F3.boolean.opBoolean","COPY",EDGE,{"derivedFrom":makeQuery(id+"F3.opExtrude","SWEPT_EDGE",EDGE,{"disambiguationData":[OSD([sQuery(id+"F0.wireOp",EDGE,"E0.bottom"),sQuery(id+"F0.wireOp",EDGE,"E0.left"),sQuery(id+"F2.wireOp",EDGE,"E56"),subQ0])]})}),makeQuery(id+"F3.boolean.opBoolean","COPY",FACE,{"derivedFrom":makeQuery(id+"F3.opExtrude","SWEPT_FACE",FACE,{"disambiguationData":[OSD([subQ0])]})})],"blendedInto":[makeQuery(id+"F3.boolean.opBoolean","COPY",FACE,{"derivedFrom":makeQuery(id+"F3.opExtrude","SWEPT_FACE",FACE,{"disambiguationData":[OSD([subQ0])]})})]});}
            var Q27;
            {var subQ0=sQuery(id+"F2.wireOp",EDGE,"E58");Q27=makeQuery(id+"F6.opChamfer","BLEND_EDGE",EDGE,{"blendedFrom":[makeQuery(id+"F3.boolean.opBoolean","COPY",EDGE,{"derivedFrom":makeQuery(id+"F3.opExtrude","SWEPT_EDGE",EDGE,{"disambiguationData":[OSD([sQuery(id+"F0.wireOp",EDGE,"E0.bottom"),sQuery(id+"F0.wireOp",EDGE,"E0.left"),subQ0,sQuery(id+"F2.wireOp",EDGE,"E59")])]})}),makeQuery(id+"F3.boolean.opBoolean","COPY",FACE,{"derivedFrom":makeQuery(id+"F3.opExtrude","SWEPT_FACE",FACE,{"disambiguationData":[OSD([subQ0])]})})],"blendedInto":[makeQuery(id+"F3.boolean.opBoolean","COPY",FACE,{"derivedFrom":makeQuery(id+"F3.opExtrude","SWEPT_FACE",FACE,{"disambiguationData":[OSD([subQ0])]})})]});}
            var Q28;
            {var subQ0=sQuery(id+"F2.wireOp",EDGE,"E60");Q28=makeQuery(id+"F6.opChamfer","BLEND_EDGE",EDGE,{"blendedFrom":[makeQuery(id+"F3.boolean.opBoolean","COPY",EDGE,{"derivedFrom":makeQuery(id+"F3.opExtrude","SWEPT_EDGE",EDGE,{"disambiguationData":[OSD([sQuery(id+"F0.wireOp",EDGE,"E0.bottom"),sQuery(id+"F0.wireOp",EDGE,"E0.left"),sQuery(id+"F2.wireOp",EDGE,"E59"),subQ0])]})}),makeQuery(id+"F3.boolean.opBoolean","COPY",FACE,{"derivedFrom":makeQuery(id+"F3.opExtrude","SWEPT_FACE",FACE,{"disambiguationData":[OSD([subQ0])]})})],"blendedInto":[makeQuery(id+"F3.boolean.opBoolean","COPY",FACE,{"derivedFrom":makeQuery(id+"F3.opExtrude","SWEPT_FACE",FACE,{"disambiguationData":[OSD([subQ0])]})})]});}
            var Q29;
            {var subQ0=sQuery(id+"F2.wireOp",EDGE,"E61");Q29=makeQuery(id+"F6.opChamfer","BLEND_EDGE",EDGE,{"blendedFrom":[makeQuery(id+"F3.boolean.opBoolean","COPY",EDGE,{"derivedFrom":makeQuery(id+"F3.opExtrude","SWEPT_EDGE",EDGE,{"disambiguationData":[OSD([sQuery(id+"F0.wireOp",EDGE,"E0.bottom"),sQuery(id+"F0.wireOp",EDGE,"E0.left"),subQ0,sQuery(id+"F2.wireOp",EDGE,"E62")])]})}),makeQuery(id+"F3.boolean.opBoolean","COPY",FACE,{"derivedFrom":makeQuery(id+"F3.opExtrude","SWEPT_FACE",FACE,{"disambiguationData":[OSD([subQ0])]})})],"blendedInto":[makeQuery(id+"F3.boolean.opBoolean","COPY",FACE,{"derivedFrom":makeQuery(id+"F3.opExtrude","SWEPT_FACE",FACE,{"disambiguationData":[OSD([subQ0])]})})]});}
            var Q30;
            {var subQ0=sQuery(id+"F2.wireOp",EDGE,"E63");Q30=makeQuery(id+"F6.opChamfer","BLEND_EDGE",EDGE,{"blendedFrom":[makeQuery(id+"F3.boolean.opBoolean","COPY",EDGE,{"derivedFrom":makeQuery(id+"F3.opExtrude","SWEPT_EDGE",EDGE,{"disambiguationData":[OSD([sQuery(id+"F2.wireOp",EDGE,"E62"),subQ0,sQuery(id+"F2.wireOp",EDGE,"E78")])]})}),makeQuery(id+"F3.boolean.opBoolean","COPY",FACE,{"derivedFrom":makeQuery(id+"F3.opExtrude","SWEPT_FACE",FACE,{"disambiguationData":[OSD([subQ0])]})})],"blendedInto":[makeQuery(id+"F3.boolean.opBoolean","COPY",FACE,{"derivedFrom":makeQuery(id+"F3.opExtrude","SWEPT_FACE",FACE,{"disambiguationData":[OSD([subQ0])]})})]});}
            var Q31;
            {var subQ0=sQuery(id+"F2.wireOp",EDGE,"E95");Q31=makeQuery(id+"F6.opChamfer","BLEND_EDGE",EDGE,{"blendedFrom":[makeQuery(id+"F3.boolean.opBoolean","COPY",EDGE,{"derivedFrom":makeQuery(id+"F3.opExtrude","SWEPT_EDGE",EDGE,{"disambiguationData":[OSD([sQuery(id+"F2.wireOp",EDGE,"E78"),subQ0])]})}),makeQuery(id+"F3.boolean.opBoolean","COPY",FACE,{"derivedFrom":makeQuery(id+"F3.opExtrude","SWEPT_FACE",FACE,{"disambiguationData":[OSD([subQ0])]})})],"blendedInto":[makeQuery(id+"F3.boolean.opBoolean","COPY",FACE,{"derivedFrom":makeQuery(id+"F3.opExtrude","SWEPT_FACE",FACE,{"disambiguationData":[OSD([subQ0])]})})]});}
            var Q32;
            {var subQ0=sQuery(id+"F2.wireOp",EDGE,"E94");Q32=makeQuery(id+"F6.opChamfer","BLEND_EDGE",EDGE,{"blendedFrom":[makeQuery(id+"F3.boolean.opBoolean","COPY",EDGE,{"derivedFrom":makeQuery(id+"F3.opExtrude","SWEPT_EDGE",EDGE,{"disambiguationData":[OSD([sQuery(id+"F2.wireOp",EDGE,"E78"),sQuery(id+"F2.wireOp",EDGE,"E93"),subQ0])]})}),makeQuery(id+"F3.boolean.opBoolean","COPY",FACE,{"derivedFrom":makeQuery(id+"F3.opExtrude","SWEPT_FACE",FACE,{"disambiguationData":[OSD([subQ0])]})})],"blendedInto":[makeQuery(id+"F3.boolean.opBoolean","COPY",FACE,{"derivedFrom":makeQuery(id+"F3.opExtrude","SWEPT_FACE",FACE,{"disambiguationData":[OSD([subQ0])]})})]});}
            var Q33;
            {var subQ0=sQuery(id+"F2.wireOp",EDGE,"E92");Q33=makeQuery(id+"F6.opChamfer","BLEND_EDGE",EDGE,{"blendedFrom":[makeQuery(id+"F3.boolean.opBoolean","COPY",EDGE,{"derivedFrom":makeQuery(id+"F3.opExtrude","SWEPT_EDGE",EDGE,{"disambiguationData":[OSD([sQuery(id+"F2.wireOp",EDGE,"E78"),subQ0,sQuery(id+"F2.wireOp",EDGE,"E93")])]})}),makeQuery(id+"F3.boolean.opBoolean","COPY",FACE,{"derivedFrom":makeQuery(id+"F3.opExtrude","SWEPT_FACE",FACE,{"disambiguationData":[OSD([subQ0])]})})],"blendedInto":[makeQuery(id+"F3.boolean.opBoolean","COPY",FACE,{"derivedFrom":makeQuery(id+"F3.opExtrude","SWEPT_FACE",FACE,{"disambiguationData":[OSD([subQ0])]})})]});}
            var Q34;
            {var subQ0=sQuery(id+"F2.wireOp",EDGE,"E91");Q34=makeQuery(id+"F6.opChamfer","BLEND_EDGE",EDGE,{"blendedFrom":[makeQuery(id+"F3.boolean.opBoolean","COPY",EDGE,{"derivedFrom":makeQuery(id+"F3.opExtrude","SWEPT_EDGE",EDGE,{"disambiguationData":[OSD([sQuery(id+"F2.wireOp",EDGE,"E78"),sQuery(id+"F2.wireOp",EDGE,"E90"),subQ0])]})}),makeQuery(id+"F3.boolean.opBoolean","COPY",FACE,{"derivedFrom":makeQuery(id+"F3.opExtrude","SWEPT_FACE",FACE,{"disambiguationData":[OSD([subQ0])]})})],"blendedInto":[makeQuery(id+"F3.boolean.opBoolean","COPY",FACE,{"derivedFrom":makeQuery(id+"F3.opExtrude","SWEPT_FACE",FACE,{"disambiguationData":[OSD([subQ0])]})})]});}
            var Q35;
            {var subQ0=sQuery(id+"F2.wireOp",EDGE,"E89");Q35=makeQuery(id+"F6.opChamfer","BLEND_EDGE",EDGE,{"blendedFrom":[makeQuery(id+"F3.boolean.opBoolean","COPY",EDGE,{"derivedFrom":makeQuery(id+"F3.opExtrude","SWEPT_EDGE",EDGE,{"disambiguationData":[OSD([sQuery(id+"F2.wireOp",EDGE,"E78"),subQ0,sQuery(id+"F2.wireOp",EDGE,"E90")])]})}),makeQuery(id+"F3.boolean.opBoolean","COPY",FACE,{"derivedFrom":makeQuery(id+"F3.opExtrude","SWEPT_FACE",FACE,{"disambiguationData":[OSD([subQ0])]})})],"blendedInto":[makeQuery(id+"F3.boolean.opBoolean","COPY",FACE,{"derivedFrom":makeQuery(id+"F3.opExtrude","SWEPT_FACE",FACE,{"disambiguationData":[OSD([subQ0])]})})]});}
            var Q36;
            {var subQ0=sQuery(id+"F2.wireOp",EDGE,"E88");Q36=makeQuery(id+"F6.opChamfer","BLEND_EDGE",EDGE,{"blendedFrom":[makeQuery(id+"F3.boolean.opBoolean","COPY",EDGE,{"derivedFrom":makeQuery(id+"F3.opExtrude","SWEPT_EDGE",EDGE,{"disambiguationData":[OSD([sQuery(id+"F2.wireOp",EDGE,"E78"),sQuery(id+"F2.wireOp",EDGE,"E87"),subQ0])]})}),makeQuery(id+"F3.boolean.opBoolean","COPY",FACE,{"derivedFrom":makeQuery(id+"F3.opExtrude","SWEPT_FACE",FACE,{"disambiguationData":[OSD([subQ0])]})})],"blendedInto":[makeQuery(id+"F3.boolean.opBoolean","COPY",FACE,{"derivedFrom":makeQuery(id+"F3.opExtrude","SWEPT_FACE",FACE,{"disambiguationData":[OSD([subQ0])]})})]});}
            var Q37;
            {var subQ0=sQuery(id+"F2.wireOp",EDGE,"E86");Q37=makeQuery(id+"F6.opChamfer","BLEND_EDGE",EDGE,{"blendedFrom":[makeQuery(id+"F3.boolean.opBoolean","COPY",EDGE,{"derivedFrom":makeQuery(id+"F3.opExtrude","SWEPT_EDGE",EDGE,{"disambiguationData":[OSD([sQuery(id+"F2.wireOp",EDGE,"E78"),subQ0,sQuery(id+"F2.wireOp",EDGE,"E87")])]})}),makeQuery(id+"F3.boolean.opBoolean","COPY",FACE,{"derivedFrom":makeQuery(id+"F3.opExtrude","SWEPT_FACE",FACE,{"disambiguationData":[OSD([subQ0])]})})],"blendedInto":[makeQuery(id+"F3.boolean.opBoolean","COPY",FACE,{"derivedFrom":makeQuery(id+"F3.opExtrude","SWEPT_FACE",FACE,{"disambiguationData":[OSD([subQ0])]})})]});}
            var Q38;
            {var subQ0=sQuery(id+"F2.wireOp",EDGE,"E85");Q38=makeQuery(id+"F6.opChamfer","BLEND_EDGE",EDGE,{"blendedFrom":[makeQuery(id+"F3.boolean.opBoolean","COPY",EDGE,{"derivedFrom":makeQuery(id+"F3.opExtrude","SWEPT_EDGE",EDGE,{"disambiguationData":[OSD([sQuery(id+"F2.wireOp",EDGE,"E78"),sQuery(id+"F2.wireOp",EDGE,"E84"),subQ0])]})}),makeQuery(id+"F3.boolean.opBoolean","COPY",FACE,{"derivedFrom":makeQuery(id+"F3.opExtrude","SWEPT_FACE",FACE,{"disambiguationData":[OSD([subQ0])]})})],"blendedInto":[makeQuery(id+"F3.boolean.opBoolean","COPY",FACE,{"derivedFrom":makeQuery(id+"F3.opExtrude","SWEPT_FACE",FACE,{"disambiguationData":[OSD([subQ0])]})})]});}
            var Q39;
            {var subQ0=sQuery(id+"F2.wireOp",EDGE,"E83");Q39=makeQuery(id+"F6.opChamfer","BLEND_EDGE",EDGE,{"blendedFrom":[makeQuery(id+"F3.boolean.opBoolean","COPY",EDGE,{"derivedFrom":makeQuery(id+"F3.opExtrude","SWEPT_EDGE",EDGE,{"disambiguationData":[OSD([sQuery(id+"F2.wireOp",EDGE,"E78"),subQ0,sQuery(id+"F2.wireOp",EDGE,"E84")])]})}),makeQuery(id+"F3.boolean.opBoolean","COPY",FACE,{"derivedFrom":makeQuery(id+"F3.opExtrude","SWEPT_FACE",FACE,{"disambiguationData":[OSD([subQ0])]})})],"blendedInto":[makeQuery(id+"F3.boolean.opBoolean","COPY",FACE,{"derivedFrom":makeQuery(id+"F3.opExtrude","SWEPT_FACE",FACE,{"disambiguationData":[OSD([subQ0])]})})]});}
            var Q40;
            {var subQ0=sQuery(id+"F2.wireOp",EDGE,"E82");Q40=makeQuery(id+"F6.opChamfer","BLEND_EDGE",EDGE,{"blendedFrom":[makeQuery(id+"F3.boolean.opBoolean","COPY",EDGE,{"derivedFrom":makeQuery(id+"F3.opExtrude","SWEPT_EDGE",EDGE,{"disambiguationData":[OSD([sQuery(id+"F2.wireOp",EDGE,"E78"),subQ0])]})}),makeQuery(id+"F3.boolean.opBoolean","COPY",FACE,{"derivedFrom":makeQuery(id+"F3.opExtrude","SWEPT_FACE",FACE,{"disambiguationData":[OSD([subQ0])]})})],"blendedInto":[makeQuery(id+"F3.boolean.opBoolean","COPY",FACE,{"derivedFrom":makeQuery(id+"F3.opExtrude","SWEPT_FACE",FACE,{"disambiguationData":[OSD([subQ0])]})})]});}
            var Q41;
            {var subQ0=sQuery(id+"F2.wireOp",EDGE,"E81");Q41=makeQuery(id+"F6.opChamfer","BLEND_EDGE",EDGE,{"blendedFrom":[makeQuery(id+"F3.boolean.opBoolean","COPY",EDGE,{"derivedFrom":makeQuery(id+"F3.opExtrude","SWEPT_EDGE",EDGE,{"disambiguationData":[OSD([sQuery(id+"F2.wireOp",EDGE,"E78"),subQ0])]})}),makeQuery(id+"F3.boolean.opBoolean","COPY",FACE,{"derivedFrom":makeQuery(id+"F3.opExtrude","SWEPT_FACE",FACE,{"disambiguationData":[OSD([subQ0])]})})],"blendedInto":[makeQuery(id+"F3.boolean.opBoolean","COPY",FACE,{"derivedFrom":makeQuery(id+"F3.opExtrude","SWEPT_FACE",FACE,{"disambiguationData":[OSD([subQ0])]})})]});}
            var Q42;
            {var subQ0=sQuery(id+"F2.wireOp",EDGE,"E39.bottom");Q42=makeQuery(id+"F6.opChamfer","BLEND_EDGE",EDGE,{"blendedFrom":[makeQuery(id+"F3.boolean.opBoolean","COPY",EDGE,{"derivedFrom":makeQuery(id+"F3.opExtrude","SWEPT_EDGE",EDGE,{"disambiguationData":[OSD([sQuery(id+"F0.wireOp",EDGE,"E0.bottom"),sQuery(id+"F0.wireOp",EDGE,"E0.left"),subQ0,sQuery(id+"F2.wireOp",EDGE,"E39.right")])]})}),makeQuery(id+"F3.boolean.opBoolean","COPY",FACE,{"derivedFrom":makeQuery(id+"F3.opExtrude","SWEPT_FACE",FACE,{"disambiguationData":[OSD([subQ0])]})})],"blendedInto":[makeQuery(id+"F3.boolean.opBoolean","COPY",FACE,{"derivedFrom":makeQuery(id+"F3.opExtrude","SWEPT_FACE",FACE,{"disambiguationData":[OSD([subQ0])]})})]});}
            var Q43;
            {var subQ0=sQuery(id+"F2.wireOp",EDGE,"E80");Q43=makeQuery(id+"F6.opChamfer","BLEND_EDGE",EDGE,{"blendedFrom":[makeQuery(id+"F3.boolean.opBoolean","COPY",EDGE,{"derivedFrom":makeQuery(id+"F3.opExtrude","SWEPT_EDGE",EDGE,{"disambiguationData":[OSD([sQuery(id+"F2.wireOp",EDGE,"E78"),subQ0])]})}),makeQuery(id+"F3.boolean.opBoolean","COPY",FACE,{"derivedFrom":makeQuery(id+"F3.opExtrude","SWEPT_FACE",FACE,{"disambiguationData":[OSD([subQ0])]})})],"blendedInto":[makeQuery(id+"F3.boolean.opBoolean","COPY",FACE,{"derivedFrom":makeQuery(id+"F3.opExtrude","SWEPT_FACE",FACE,{"disambiguationData":[OSD([subQ0])]})})]});}
            var Q44;
            {var subQ0=sQuery(id+"F2.wireOp",EDGE,"E79");Q44=makeQuery(id+"F6.opChamfer","BLEND_EDGE",EDGE,{"blendedFrom":[makeQuery(id+"F3.boolean.opBoolean","COPY",EDGE,{"derivedFrom":makeQuery(id+"F3.opExtrude","SWEPT_EDGE",EDGE,{"disambiguationData":[OSD([sQuery(id+"F0.wireOp",EDGE,"E0.bottom"),sQuery(id+"F0.wireOp",EDGE,"E0.left"),sQuery(id+"F2.wireOp",EDGE,"E78"),subQ0])]})}),makeQuery(id+"F3.boolean.opBoolean","COPY",FACE,{"derivedFrom":makeQuery(id+"F3.opExtrude","SWEPT_FACE",FACE,{"disambiguationData":[OSD([subQ0])]})})],"blendedInto":[makeQuery(id+"F3.boolean.opBoolean","COPY",FACE,{"derivedFrom":makeQuery(id+"F3.opExtrude","SWEPT_FACE",FACE,{"disambiguationData":[OSD([subQ0])]})})]});}
            var Q45;
            {var subQ0=sQuery(id+"F2.wireOp",EDGE,"E97");Q45=makeQuery(id+"F6.opChamfer","BLEND_EDGE",EDGE,{"blendedFrom":[makeQuery(id+"F3.boolean.opBoolean","COPY",EDGE,{"derivedFrom":makeQuery(id+"F3.opExtrude","SWEPT_EDGE",EDGE,{"disambiguationData":[OSD([sQuery(id+"F0.wireOp",EDGE,"E0.bottom"),sQuery(id+"F0.wireOp",EDGE,"E0.left"),subQ0,sQuery(id+"F2.wireOp",EDGE,"E98")])]})}),makeQuery(id+"F3.boolean.opBoolean","COPY",FACE,{"derivedFrom":makeQuery(id+"F3.opExtrude","SWEPT_FACE",FACE,{"disambiguationData":[OSD([subQ0])]})})],"blendedInto":[makeQuery(id+"F3.boolean.opBoolean","COPY",FACE,{"derivedFrom":makeQuery(id+"F3.opExtrude","SWEPT_FACE",FACE,{"disambiguationData":[OSD([subQ0])]})})]});}
            var Q46;
            {var subQ0=sQuery(id+"F2.wireOp",EDGE,"E99");Q46=makeQuery(id+"F6.opChamfer","BLEND_EDGE",EDGE,{"blendedFrom":[makeQuery(id+"F3.boolean.opBoolean","COPY",EDGE,{"derivedFrom":makeQuery(id+"F3.opExtrude","SWEPT_EDGE",EDGE,{"disambiguationData":[OSD([sQuery(id+"F0.wireOp",EDGE,"E0.bottom"),sQuery(id+"F0.wireOp",EDGE,"E0.left"),sQuery(id+"F2.wireOp",EDGE,"E98"),subQ0])]})}),makeQuery(id+"F3.boolean.opBoolean","COPY",FACE,{"derivedFrom":makeQuery(id+"F3.opExtrude","SWEPT_FACE",FACE,{"disambiguationData":[OSD([subQ0])]})})],"blendedInto":[makeQuery(id+"F3.boolean.opBoolean","COPY",FACE,{"derivedFrom":makeQuery(id+"F3.opExtrude","SWEPT_FACE",FACE,{"disambiguationData":[OSD([subQ0])]})})]});}
            var Q47;
            {var subQ0=sQuery(id+"F2.wireOp",EDGE,"E101");Q47=makeQuery(id+"F6.opChamfer","BLEND_EDGE",EDGE,{"blendedFrom":[makeQuery(id+"F3.boolean.opBoolean","COPY",EDGE,{"derivedFrom":makeQuery(id+"F3.opExtrude","SWEPT_EDGE",EDGE,{"disambiguationData":[OSD([sQuery(id+"F0.wireOp",EDGE,"E0.bottom"),sQuery(id+"F0.wireOp",EDGE,"E0.left"),subQ0,sQuery(id+"F2.wireOp",EDGE,"E102")])]})}),makeQuery(id+"F3.boolean.opBoolean","COPY",FACE,{"derivedFrom":makeQuery(id+"F3.opExtrude","SWEPT_FACE",FACE,{"disambiguationData":[OSD([subQ0])]})})],"blendedInto":[makeQuery(id+"F3.boolean.opBoolean","COPY",FACE,{"derivedFrom":makeQuery(id+"F3.opExtrude","SWEPT_FACE",FACE,{"disambiguationData":[OSD([subQ0])]})})]});}
            var Q48;
            {var subQ0=sQuery(id+"F2.wireOp",EDGE,"E103");Q48=makeQuery(id+"F6.opChamfer","BLEND_EDGE",EDGE,{"blendedFrom":[makeQuery(id+"F3.boolean.opBoolean","COPY",EDGE,{"derivedFrom":makeQuery(id+"F3.opExtrude","SWEPT_EDGE",EDGE,{"disambiguationData":[OSD([sQuery(id+"F0.wireOp",EDGE,"E0.bottom"),sQuery(id+"F0.wireOp",EDGE,"E0.left"),sQuery(id+"F2.wireOp",EDGE,"E102"),subQ0])]})}),makeQuery(id+"F3.boolean.opBoolean","COPY",FACE,{"derivedFrom":makeQuery(id+"F3.opExtrude","SWEPT_FACE",FACE,{"disambiguationData":[OSD([subQ0])]})})],"blendedInto":[makeQuery(id+"F3.boolean.opBoolean","COPY",FACE,{"derivedFrom":makeQuery(id+"F3.opExtrude","SWEPT_FACE",FACE,{"disambiguationData":[OSD([subQ0])]})})]});}
            var Q49;
            {var subQ0=sQuery(id+"F2.wireOp",EDGE,"E105");Q49=makeQuery(id+"F6.opChamfer","BLEND_EDGE",EDGE,{"blendedFrom":[makeQuery(id+"F3.boolean.opBoolean","COPY",EDGE,{"derivedFrom":makeQuery(id+"F3.opExtrude","SWEPT_EDGE",EDGE,{"disambiguationData":[OSD([sQuery(id+"F0.wireOp",EDGE,"E0.bottom"),sQuery(id+"F0.wireOp",EDGE,"E0.left"),subQ0,sQuery(id+"F2.wireOp",EDGE,"E106")])]})}),makeQuery(id+"F3.boolean.opBoolean","COPY",FACE,{"derivedFrom":makeQuery(id+"F3.opExtrude","SWEPT_FACE",FACE,{"disambiguationData":[OSD([subQ0])]})})],"blendedInto":[makeQuery(id+"F3.boolean.opBoolean","COPY",FACE,{"derivedFrom":makeQuery(id+"F3.opExtrude","SWEPT_FACE",FACE,{"disambiguationData":[OSD([subQ0])]})})]});}
            var Q50;
            {var subQ0=sQuery(id+"F2.wireOp",EDGE,"E107");Q50=makeQuery(id+"F6.opChamfer","BLEND_EDGE",EDGE,{"blendedFrom":[makeQuery(id+"F3.boolean.opBoolean","COPY",EDGE,{"derivedFrom":makeQuery(id+"F3.opExtrude","SWEPT_EDGE",EDGE,{"disambiguationData":[OSD([sQuery(id+"F0.wireOp",EDGE,"E0.bottom"),sQuery(id+"F0.wireOp",EDGE,"E0.left"),sQuery(id+"F2.wireOp",EDGE,"E106"),subQ0])]})}),makeQuery(id+"F3.boolean.opBoolean","COPY",FACE,{"derivedFrom":makeQuery(id+"F3.opExtrude","SWEPT_FACE",FACE,{"disambiguationData":[OSD([subQ0])]})})],"blendedInto":[makeQuery(id+"F3.boolean.opBoolean","COPY",FACE,{"derivedFrom":makeQuery(id+"F3.opExtrude","SWEPT_FACE",FACE,{"disambiguationData":[OSD([subQ0])]})})]});}
            var Q51;
            {var subQ0=sQuery(id+"F2.wireOp",EDGE,"E109");Q51=makeQuery(id+"F6.opChamfer","BLEND_EDGE",EDGE,{"blendedFrom":[makeQuery(id+"F3.boolean.opBoolean","COPY",EDGE,{"derivedFrom":makeQuery(id+"F3.opExtrude","SWEPT_EDGE",EDGE,{"disambiguationData":[OSD([sQuery(id+"F0.wireOp",EDGE,"E0.bottom"),sQuery(id+"F0.wireOp",EDGE,"E0.left"),subQ0,sQuery(id+"F2.wireOp",EDGE,"E110")])]})}),makeQuery(id+"F3.boolean.opBoolean","COPY",FACE,{"derivedFrom":makeQuery(id+"F3.opExtrude","SWEPT_FACE",FACE,{"disambiguationData":[OSD([subQ0])]})})],"blendedInto":[makeQuery(id+"F3.boolean.opBoolean","COPY",FACE,{"derivedFrom":makeQuery(id+"F3.opExtrude","SWEPT_FACE",FACE,{"disambiguationData":[OSD([subQ0])]})})]});}
            var Q52;
            {var subQ0=sQuery(id+"F2.wireOp",EDGE,"E64.MirrorCS");Q52=makeQuery(id+"F6.opChamfer","BLEND_EDGE",EDGE,{"blendedFrom":[makeQuery(id+"F3.boolean.opBoolean","COPY",EDGE,{"derivedFrom":makeQuery(id+"F3.opExtrude","SWEPT_EDGE",EDGE,{"disambiguationData":[OSD([sQuery(id+"F0.wireOp",EDGE,"E0.bottom"),sQuery(id+"F0.wireOp",EDGE,"E0.left"),subQ0])]})}),makeQuery(id+"F3.boolean.opBoolean","COPY",FACE,{"derivedFrom":makeQuery(id+"F3.opExtrude","SWEPT_FACE",FACE,{"disambiguationData":[OSD([subQ0])]})})],"blendedInto":[makeQuery(id+"F3.boolean.opBoolean","COPY",FACE,{"derivedFrom":makeQuery(id+"F3.opExtrude","SWEPT_FACE",FACE,{"disambiguationData":[OSD([subQ0])]})})]});}
            var Q53;
            {var subQ0=sQuery(id+"F2.wireOp",EDGE,"E111");Q53=makeQuery(id+"F6.opChamfer","BLEND_EDGE",EDGE,{"blendedFrom":[makeQuery(id+"F3.boolean.opBoolean","COPY",EDGE,{"derivedFrom":makeQuery(id+"F3.opExtrude","SWEPT_EDGE",EDGE,{"disambiguationData":[OSD([sQuery(id+"F0.wireOp",EDGE,"E0.bottom"),sQuery(id+"F0.wireOp",EDGE,"E0.left"),sQuery(id+"F2.wireOp",EDGE,"E110"),subQ0])]})}),makeQuery(id+"F3.boolean.opBoolean","COPY",FACE,{"derivedFrom":makeQuery(id+"F3.opExtrude","SWEPT_FACE",FACE,{"disambiguationData":[OSD([subQ0])]})})],"blendedInto":[makeQuery(id+"F3.boolean.opBoolean","COPY",FACE,{"derivedFrom":makeQuery(id+"F3.opExtrude","SWEPT_FACE",FACE,{"disambiguationData":[OSD([subQ0])]})})]});}
            var Q54;
            {var subQ0=sQuery(id+"F2.wireOp",EDGE,"E113");Q54=makeQuery(id+"F6.opChamfer","BLEND_EDGE",EDGE,{"blendedFrom":[makeQuery(id+"F3.boolean.opBoolean","COPY",EDGE,{"derivedFrom":makeQuery(id+"F3.opExtrude","SWEPT_EDGE",EDGE,{"disambiguationData":[OSD([sQuery(id+"F0.wireOp",EDGE,"E0.bottom"),sQuery(id+"F0.wireOp",EDGE,"E0.left"),subQ0,sQuery(id+"F2.wireOp",EDGE,"E114")])]})}),makeQuery(id+"F3.boolean.opBoolean","COPY",FACE,{"derivedFrom":makeQuery(id+"F3.opExtrude","SWEPT_FACE",FACE,{"disambiguationData":[OSD([subQ0])]})})],"blendedInto":[makeQuery(id+"F3.boolean.opBoolean","COPY",FACE,{"derivedFrom":makeQuery(id+"F3.opExtrude","SWEPT_FACE",FACE,{"disambiguationData":[OSD([subQ0])]})})]});}
            var Q55;
            {var subQ0=sQuery(id+"F2.wireOp",EDGE,"E115");Q55=makeQuery(id+"F6.opChamfer","BLEND_EDGE",EDGE,{"blendedFrom":[makeQuery(id+"F3.boolean.opBoolean","COPY",EDGE,{"derivedFrom":makeQuery(id+"F3.opExtrude","SWEPT_EDGE",EDGE,{"disambiguationData":[OSD([sQuery(id+"F0.wireOp",EDGE,"E0.bottom"),sQuery(id+"F0.wireOp",EDGE,"E0.left"),sQuery(id+"F2.wireOp",EDGE,"E114"),subQ0])]})}),makeQuery(id+"F3.boolean.opBoolean","COPY",FACE,{"derivedFrom":makeQuery(id+"F3.opExtrude","SWEPT_FACE",FACE,{"disambiguationData":[OSD([subQ0])]})})],"blendedInto":[makeQuery(id+"F3.boolean.opBoolean","COPY",FACE,{"derivedFrom":makeQuery(id+"F3.opExtrude","SWEPT_FACE",FACE,{"disambiguationData":[OSD([subQ0])]})})]});}
            var Q56;
            {var subQ0=sQuery(id+"F2.wireOp",EDGE,"E117");Q56=makeQuery(id+"F6.opChamfer","BLEND_EDGE",EDGE,{"blendedFrom":[makeQuery(id+"F3.boolean.opBoolean","COPY",EDGE,{"derivedFrom":makeQuery(id+"F3.opExtrude","SWEPT_EDGE",EDGE,{"disambiguationData":[OSD([sQuery(id+"F0.wireOp",EDGE,"E0.bottom"),sQuery(id+"F0.wireOp",EDGE,"E0.left"),subQ0,sQuery(id+"F2.wireOp",EDGE,"E118")])]})}),makeQuery(id+"F3.boolean.opBoolean","COPY",FACE,{"derivedFrom":makeQuery(id+"F3.opExtrude","SWEPT_FACE",FACE,{"disambiguationData":[OSD([subQ0])]})})],"blendedInto":[makeQuery(id+"F3.boolean.opBoolean","COPY",FACE,{"derivedFrom":makeQuery(id+"F3.opExtrude","SWEPT_FACE",FACE,{"disambiguationData":[OSD([subQ0])]})})]});}
            var Q57;
            {var subQ0=sQuery(id+"F2.wireOp",EDGE,"E125");Q57=makeQuery(id+"F6.opChamfer","BLEND_EDGE",EDGE,{"blendedFrom":[makeQuery(id+"F3.boolean.opBoolean","COPY",EDGE,{"derivedFrom":makeQuery(id+"F3.opExtrude","SWEPT_EDGE",EDGE,{"disambiguationData":[OSD([sQuery(id+"F0.wireOp",EDGE,"E0.bottom"),sQuery(id+"F0.wireOp",EDGE,"E0.left"),subQ0,sQuery(id+"F2.wireOp",EDGE,"E126")])]})}),makeQuery(id+"F3.boolean.opBoolean","COPY",FACE,{"derivedFrom":makeQuery(id+"F3.opExtrude","SWEPT_FACE",FACE,{"disambiguationData":[OSD([subQ0])]})})],"blendedInto":[makeQuery(id+"F3.boolean.opBoolean","COPY",FACE,{"derivedFrom":makeQuery(id+"F3.opExtrude","SWEPT_FACE",FACE,{"disambiguationData":[OSD([subQ0])]})})]});}
            var Q58;
            {var subQ0=sQuery(id+"F2.wireOp",EDGE,"E123");Q58=makeQuery(id+"F6.opChamfer","BLEND_EDGE",EDGE,{"blendedFrom":[makeQuery(id+"F3.boolean.opBoolean","COPY",EDGE,{"derivedFrom":makeQuery(id+"F3.opExtrude","SWEPT_EDGE",EDGE,{"disambiguationData":[OSD([sQuery(id+"F0.wireOp",EDGE,"E0.bottom"),sQuery(id+"F0.wireOp",EDGE,"E0.left"),sQuery(id+"F2.wireOp",EDGE,"E122"),subQ0])]})}),makeQuery(id+"F3.boolean.opBoolean","COPY",FACE,{"derivedFrom":makeQuery(id+"F3.opExtrude","SWEPT_FACE",FACE,{"disambiguationData":[OSD([subQ0])]})})],"blendedInto":[makeQuery(id+"F3.boolean.opBoolean","COPY",FACE,{"derivedFrom":makeQuery(id+"F3.opExtrude","SWEPT_FACE",FACE,{"disambiguationData":[OSD([subQ0])]})})]});}
            var Q59;
            {var subQ0=sQuery(id+"F2.wireOp",EDGE,"E127");Q59=makeQuery(id+"F6.opChamfer","BLEND_EDGE",EDGE,{"blendedFrom":[makeQuery(id+"F3.boolean.opBoolean","COPY",EDGE,{"derivedFrom":makeQuery(id+"F3.opExtrude","SWEPT_EDGE",EDGE,{"disambiguationData":[OSD([sQuery(id+"F0.wireOp",EDGE,"E0.bottom"),sQuery(id+"F0.wireOp",EDGE,"E0.left"),sQuery(id+"F2.wireOp",EDGE,"E126"),subQ0])]})}),makeQuery(id+"F3.boolean.opBoolean","COPY",FACE,{"derivedFrom":makeQuery(id+"F3.opExtrude","SWEPT_FACE",FACE,{"disambiguationData":[OSD([subQ0])]})})],"blendedInto":[makeQuery(id+"F3.boolean.opBoolean","COPY",FACE,{"derivedFrom":makeQuery(id+"F3.opExtrude","SWEPT_FACE",FACE,{"disambiguationData":[OSD([subQ0])]})})]});}
            var Q60;
            {var subQ0=sQuery(id+"F2.wireOp",EDGE,"E129");Q60=makeQuery(id+"F6.opChamfer","BLEND_EDGE",EDGE,{"blendedFrom":[makeQuery(id+"F3.boolean.opBoolean","COPY",EDGE,{"derivedFrom":makeQuery(id+"F3.opExtrude","SWEPT_EDGE",EDGE,{"disambiguationData":[OSD([sQuery(id+"F0.wireOp",EDGE,"E0.bottom"),sQuery(id+"F0.wireOp",EDGE,"E0.left"),subQ0,sQuery(id+"F2.wireOp",EDGE,"E130")])]})}),makeQuery(id+"F3.boolean.opBoolean","COPY",FACE,{"derivedFrom":makeQuery(id+"F3.opExtrude","SWEPT_FACE",FACE,{"disambiguationData":[OSD([subQ0])]})})],"blendedInto":[makeQuery(id+"F3.boolean.opBoolean","COPY",FACE,{"derivedFrom":makeQuery(id+"F3.opExtrude","SWEPT_FACE",FACE,{"disambiguationData":[OSD([subQ0])]})})]});}
            var Q61;
            {var subQ0=sQuery(id+"F2.wireOp",EDGE,"E121");Q61=makeQuery(id+"F6.opChamfer","BLEND_EDGE",EDGE,{"blendedFrom":[makeQuery(id+"F3.boolean.opBoolean","COPY",EDGE,{"derivedFrom":makeQuery(id+"F3.opExtrude","SWEPT_EDGE",EDGE,{"disambiguationData":[OSD([sQuery(id+"F0.wireOp",EDGE,"E0.bottom"),sQuery(id+"F0.wireOp",EDGE,"E0.left"),subQ0,sQuery(id+"F2.wireOp",EDGE,"E122")])]})}),makeQuery(id+"F3.boolean.opBoolean","COPY",FACE,{"derivedFrom":makeQuery(id+"F3.opExtrude","SWEPT_FACE",FACE,{"disambiguationData":[OSD([subQ0])]})})],"blendedInto":[makeQuery(id+"F3.boolean.opBoolean","COPY",FACE,{"derivedFrom":makeQuery(id+"F3.opExtrude","SWEPT_FACE",FACE,{"disambiguationData":[OSD([subQ0])]})})]});}
            var Q62;
            {var subQ0=sQuery(id+"F2.wireOp",EDGE,"E119");Q62=makeQuery(id+"F6.opChamfer","BLEND_EDGE",EDGE,{"blendedFrom":[makeQuery(id+"F3.boolean.opBoolean","COPY",EDGE,{"derivedFrom":makeQuery(id+"F3.opExtrude","SWEPT_EDGE",EDGE,{"disambiguationData":[OSD([sQuery(id+"F0.wireOp",EDGE,"E0.bottom"),sQuery(id+"F0.wireOp",EDGE,"E0.left"),sQuery(id+"F2.wireOp",EDGE,"E118"),subQ0])]})}),makeQuery(id+"F3.boolean.opBoolean","COPY",FACE,{"derivedFrom":makeQuery(id+"F3.opExtrude","SWEPT_FACE",FACE,{"disambiguationData":[OSD([subQ0])]})})],"blendedInto":[makeQuery(id+"F3.boolean.opBoolean","COPY",FACE,{"derivedFrom":makeQuery(id+"F3.opExtrude","SWEPT_FACE",FACE,{"disambiguationData":[OSD([subQ0])]})})]});}
            var Q63;
            {var subQ0=sQuery(id+"F2.wireOp",EDGE,"E131");Q63=makeQuery(id+"F6.opChamfer","BLEND_EDGE",EDGE,{"blendedFrom":[makeQuery(id+"F3.boolean.opBoolean","COPY",EDGE,{"derivedFrom":makeQuery(id+"F3.opExtrude","SWEPT_EDGE",EDGE,{"disambiguationData":[OSD([sQuery(id+"F0.wireOp",EDGE,"E0.bottom"),sQuery(id+"F0.wireOp",EDGE,"E0.left"),sQuery(id+"F2.wireOp",EDGE,"E130"),subQ0])]})}),makeQuery(id+"F3.boolean.opBoolean","COPY",FACE,{"derivedFrom":makeQuery(id+"F3.opExtrude","SWEPT_FACE",FACE,{"disambiguationData":[OSD([subQ0])]})})],"blendedInto":[makeQuery(id+"F3.boolean.opBoolean","COPY",FACE,{"derivedFrom":makeQuery(id+"F3.opExtrude","SWEPT_FACE",FACE,{"disambiguationData":[OSD([subQ0])]})})]});}
            var Q64;
            {var subQ0=sQuery(id+"F2.wireOp",EDGE,"E133");Q64=makeQuery(id+"F6.opChamfer","BLEND_EDGE",EDGE,{"blendedFrom":[makeQuery(id+"F3.boolean.opBoolean","COPY",EDGE,{"derivedFrom":makeQuery(id+"F3.opExtrude","SWEPT_EDGE",EDGE,{"disambiguationData":[OSD([sQuery(id+"F0.wireOp",EDGE,"E0.bottom"),sQuery(id+"F0.wireOp",EDGE,"E0.left"),subQ0,sQuery(id+"F2.wireOp",EDGE,"E134")])]})}),makeQuery(id+"F3.boolean.opBoolean","COPY",FACE,{"derivedFrom":makeQuery(id+"F3.opExtrude","SWEPT_FACE",FACE,{"disambiguationData":[OSD([subQ0])]})})],"blendedInto":[makeQuery(id+"F3.boolean.opBoolean","COPY",FACE,{"derivedFrom":makeQuery(id+"F3.opExtrude","SWEPT_FACE",FACE,{"disambiguationData":[OSD([subQ0])]})})]});}
            var Q65;
            {var subQ0=sQuery(id+"F2.wireOp",EDGE,"E141");Q65=makeQuery(id+"F6.opChamfer","BLEND_EDGE",EDGE,{"blendedFrom":[makeQuery(id+"F3.boolean.opBoolean","COPY",EDGE,{"derivedFrom":makeQuery(id+"F3.opExtrude","SWEPT_EDGE",EDGE,{"disambiguationData":[OSD([sQuery(id+"F0.wireOp",EDGE,"E0.bottom"),sQuery(id+"F0.wireOp",EDGE,"E0.left"),subQ0,sQuery(id+"F2.wireOp",EDGE,"E142")])]})}),makeQuery(id+"F3.boolean.opBoolean","COPY",FACE,{"derivedFrom":makeQuery(id+"F3.opExtrude","SWEPT_FACE",FACE,{"disambiguationData":[OSD([subQ0])]})})],"blendedInto":[makeQuery(id+"F3.boolean.opBoolean","COPY",FACE,{"derivedFrom":makeQuery(id+"F3.opExtrude","SWEPT_FACE",FACE,{"disambiguationData":[OSD([subQ0])]})})]});}
            var Q66;
            {var subQ0=sQuery(id+"F2.wireOp",EDGE,"E139");Q66=makeQuery(id+"F6.opChamfer","BLEND_EDGE",EDGE,{"blendedFrom":[makeQuery(id+"F3.boolean.opBoolean","COPY",EDGE,{"derivedFrom":makeQuery(id+"F3.opExtrude","SWEPT_EDGE",EDGE,{"disambiguationData":[OSD([sQuery(id+"F0.wireOp",EDGE,"E0.bottom"),sQuery(id+"F0.wireOp",EDGE,"E0.left"),sQuery(id+"F2.wireOp",EDGE,"E138"),subQ0])]})}),makeQuery(id+"F3.boolean.opBoolean","COPY",FACE,{"derivedFrom":makeQuery(id+"F3.opExtrude","SWEPT_FACE",FACE,{"disambiguationData":[OSD([subQ0])]})})],"blendedInto":[makeQuery(id+"F3.boolean.opBoolean","COPY",FACE,{"derivedFrom":makeQuery(id+"F3.opExtrude","SWEPT_FACE",FACE,{"disambiguationData":[OSD([subQ0])]})})]});}
            var Q67;
            {var subQ0=sQuery(id+"F2.wireOp",EDGE,"E143");Q67=makeQuery(id+"F6.opChamfer","BLEND_EDGE",EDGE,{"blendedFrom":[makeQuery(id+"F3.boolean.opBoolean","COPY",EDGE,{"derivedFrom":makeQuery(id+"F3.opExtrude","SWEPT_EDGE",EDGE,{"disambiguationData":[OSD([sQuery(id+"F0.wireOp",EDGE,"E0.bottom"),sQuery(id+"F0.wireOp",EDGE,"E0.left"),sQuery(id+"F2.wireOp",EDGE,"E142"),subQ0])]})}),makeQuery(id+"F3.boolean.opBoolean","COPY",FACE,{"derivedFrom":makeQuery(id+"F3.opExtrude","SWEPT_FACE",FACE,{"disambiguationData":[OSD([subQ0])]})})],"blendedInto":[makeQuery(id+"F3.boolean.opBoolean","COPY",FACE,{"derivedFrom":makeQuery(id+"F3.opExtrude","SWEPT_FACE",FACE,{"disambiguationData":[OSD([subQ0])]})})]});}
            var Q68;
            {var subQ0=sQuery(id+"F2.wireOp",EDGE,"E145");Q68=makeQuery(id+"F6.opChamfer","BLEND_EDGE",EDGE,{"blendedFrom":[makeQuery(id+"F3.boolean.opBoolean","COPY",EDGE,{"derivedFrom":makeQuery(id+"F3.opExtrude","SWEPT_EDGE",EDGE,{"disambiguationData":[OSD([sQuery(id+"F0.wireOp",EDGE,"E0.bottom"),sQuery(id+"F0.wireOp",EDGE,"E0.left"),subQ0,sQuery(id+"F2.wireOp",EDGE,"E146")])]})}),makeQuery(id+"F3.boolean.opBoolean","COPY",FACE,{"derivedFrom":makeQuery(id+"F3.opExtrude","SWEPT_FACE",FACE,{"disambiguationData":[OSD([subQ0])]})})],"blendedInto":[makeQuery(id+"F3.boolean.opBoolean","COPY",FACE,{"derivedFrom":makeQuery(id+"F3.opExtrude","SWEPT_FACE",FACE,{"disambiguationData":[OSD([subQ0])]})})]});}
            var Q69;
            {var subQ0=sQuery(id+"F2.wireOp",EDGE,"E149");Q69=makeQuery(id+"F6.opChamfer","BLEND_EDGE",EDGE,{"blendedFrom":[makeQuery(id+"F3.boolean.opBoolean","COPY",EDGE,{"derivedFrom":makeQuery(id+"F3.opExtrude","SWEPT_EDGE",EDGE,{"disambiguationData":[OSD([sQuery(id+"F0.wireOp",EDGE,"E0.bottom"),sQuery(id+"F0.wireOp",EDGE,"E0.left"),subQ0,sQuery(id+"F2.wireOp",EDGE,"E150")])]})}),makeQuery(id+"F3.boolean.opBoolean","COPY",FACE,{"derivedFrom":makeQuery(id+"F3.opExtrude","SWEPT_FACE",FACE,{"disambiguationData":[OSD([subQ0])]})})],"blendedInto":[makeQuery(id+"F3.boolean.opBoolean","COPY",FACE,{"derivedFrom":makeQuery(id+"F3.opExtrude","SWEPT_FACE",FACE,{"disambiguationData":[OSD([subQ0])]})})]});}
            var Q70;
            {var subQ0=sQuery(id+"F2.wireOp",EDGE,"E147");Q70=makeQuery(id+"F6.opChamfer","BLEND_EDGE",EDGE,{"blendedFrom":[makeQuery(id+"F3.boolean.opBoolean","COPY",EDGE,{"derivedFrom":makeQuery(id+"F3.opExtrude","SWEPT_EDGE",EDGE,{"disambiguationData":[OSD([sQuery(id+"F0.wireOp",EDGE,"E0.bottom"),sQuery(id+"F0.wireOp",EDGE,"E0.left"),sQuery(id+"F2.wireOp",EDGE,"E146"),subQ0])]})}),makeQuery(id+"F3.boolean.opBoolean","COPY",FACE,{"derivedFrom":makeQuery(id+"F3.opExtrude","SWEPT_FACE",FACE,{"disambiguationData":[OSD([subQ0])]})})],"blendedInto":[makeQuery(id+"F3.boolean.opBoolean","COPY",FACE,{"derivedFrom":makeQuery(id+"F3.opExtrude","SWEPT_FACE",FACE,{"disambiguationData":[OSD([subQ0])]})})]});}
            var Q71;
            {var subQ0=sQuery(id+"F2.wireOp",EDGE,"E151");Q71=makeQuery(id+"F9.opChamfer","BLEND_EDGE",EDGE,{"blendedFrom":[makeQuery(id+"F3.boolean.opBoolean","COPY",EDGE,{"derivedFrom":makeQuery(id+"F3.opExtrude","SWEPT_EDGE",EDGE,{"disambiguationData":[OSD([sQuery(id+"F0.wireOp",EDGE,"E0.bottom"),sQuery(id+"F0.wireOp",EDGE,"E0.left"),sQuery(id+"F2.wireOp",EDGE,"E150"),subQ0])]})}),makeQuery(id+"F3.boolean.opBoolean","COPY",FACE,{"derivedFrom":makeQuery(id+"F3.opExtrude","SWEPT_FACE",FACE,{"disambiguationData":[OSD([subQ0])]})})],"blendedInto":[makeQuery(id+"F3.boolean.opBoolean","COPY",FACE,{"derivedFrom":makeQuery(id+"F3.opExtrude","SWEPT_FACE",FACE,{"disambiguationData":[OSD([subQ0])]})})]});}
            var Q72;
            {var subQ0=sQuery(id+"F7.wireOp",EDGE,"E152.top");Q72=makeQuery(id+"F9.opChamfer","BLEND_EDGE",EDGE,{"blendedFrom":[makeQuery(id+"F8.boolean.opBoolean","COPY",EDGE,{"derivedFrom":makeQuery(id+"F8.opExtrude","CAP_EDGE",EDGE,{"disambiguationData":[OSD([subQ0])],"isStart":true})}),makeQuery(id+"F8.boolean.opBoolean","COPY",FACE,{"derivedFrom":makeQuery(id+"F8.opExtrude","SWEPT_FACE",FACE,{"disambiguationData":[OSD([subQ0])]})})],"blendedInto":[makeQuery(id+"F8.boolean.opBoolean","COPY",FACE,{"derivedFrom":makeQuery(id+"F8.opExtrude","SWEPT_FACE",FACE,{"disambiguationData":[OSD([subQ0])]})})]});}
            var Q73;
            {var subQ0=sQuery(id+"F2.wireOp",EDGE,"E137");Q73=makeQuery(id+"F6.opChamfer","BLEND_EDGE",EDGE,{"blendedFrom":[makeQuery(id+"F3.boolean.opBoolean","COPY",EDGE,{"derivedFrom":makeQuery(id+"F3.opExtrude","SWEPT_EDGE",EDGE,{"disambiguationData":[OSD([sQuery(id+"F0.wireOp",EDGE,"E0.bottom"),sQuery(id+"F0.wireOp",EDGE,"E0.left"),subQ0,sQuery(id+"F2.wireOp",EDGE,"E138")])]})}),makeQuery(id+"F3.boolean.opBoolean","COPY",FACE,{"derivedFrom":makeQuery(id+"F3.opExtrude","SWEPT_FACE",FACE,{"disambiguationData":[OSD([subQ0])]})})],"blendedInto":[makeQuery(id+"F3.boolean.opBoolean","COPY",FACE,{"derivedFrom":makeQuery(id+"F3.opExtrude","SWEPT_FACE",FACE,{"disambiguationData":[OSD([subQ0])]})})]});}
            var Q74;
            {var subQ0=sQuery(id+"F2.wireOp",EDGE,"E135");Q74=makeQuery(id+"F6.opChamfer","BLEND_EDGE",EDGE,{"blendedFrom":[makeQuery(id+"F3.boolean.opBoolean","COPY",EDGE,{"derivedFrom":makeQuery(id+"F3.opExtrude","SWEPT_EDGE",EDGE,{"disambiguationData":[OSD([sQuery(id+"F0.wireOp",EDGE,"E0.bottom"),sQuery(id+"F0.wireOp",EDGE,"E0.left"),sQuery(id+"F2.wireOp",EDGE,"E134"),subQ0])]})}),makeQuery(id+"F3.boolean.opBoolean","COPY",FACE,{"derivedFrom":makeQuery(id+"F3.opExtrude","SWEPT_FACE",FACE,{"disambiguationData":[OSD([subQ0])]})})],"blendedInto":[makeQuery(id+"F3.boolean.opBoolean","COPY",FACE,{"derivedFrom":makeQuery(id+"F3.opExtrude","SWEPT_FACE",FACE,{"disambiguationData":[OSD([subQ0])]})})]});}
            chamfer(context, id + "F10", {"entities" : qUnion([Q0, Q1, Q2, Q3, Q4, Q5, Q6, Q7, Q8, Q9, Q10, Q11, Q12, Q13, Q14, Q15, Q16, Q17, Q18, Q19, Q20, Q21, Q22, Q23, Q24, Q25, Q26, Q27, Q28, Q29, Q30, Q31, Q32, Q33, Q34, Q35, Q36, Q37, Q38, Q39, Q40, Q41, Q42, Q43, Q44, Q45, Q46, Q47, Q48, Q49, Q50, Q51, Q52, Q53, Q54, Q55, Q56, Q57, Q58, Q59, Q60, Q61, Q62, Q63, Q64, Q65, Q66, Q67, Q68, Q69, Q70, Q71, Q72, Q73, Q74]), "width" : 1.27 * mm, "tangentPropagation" : true});
        }
    });
